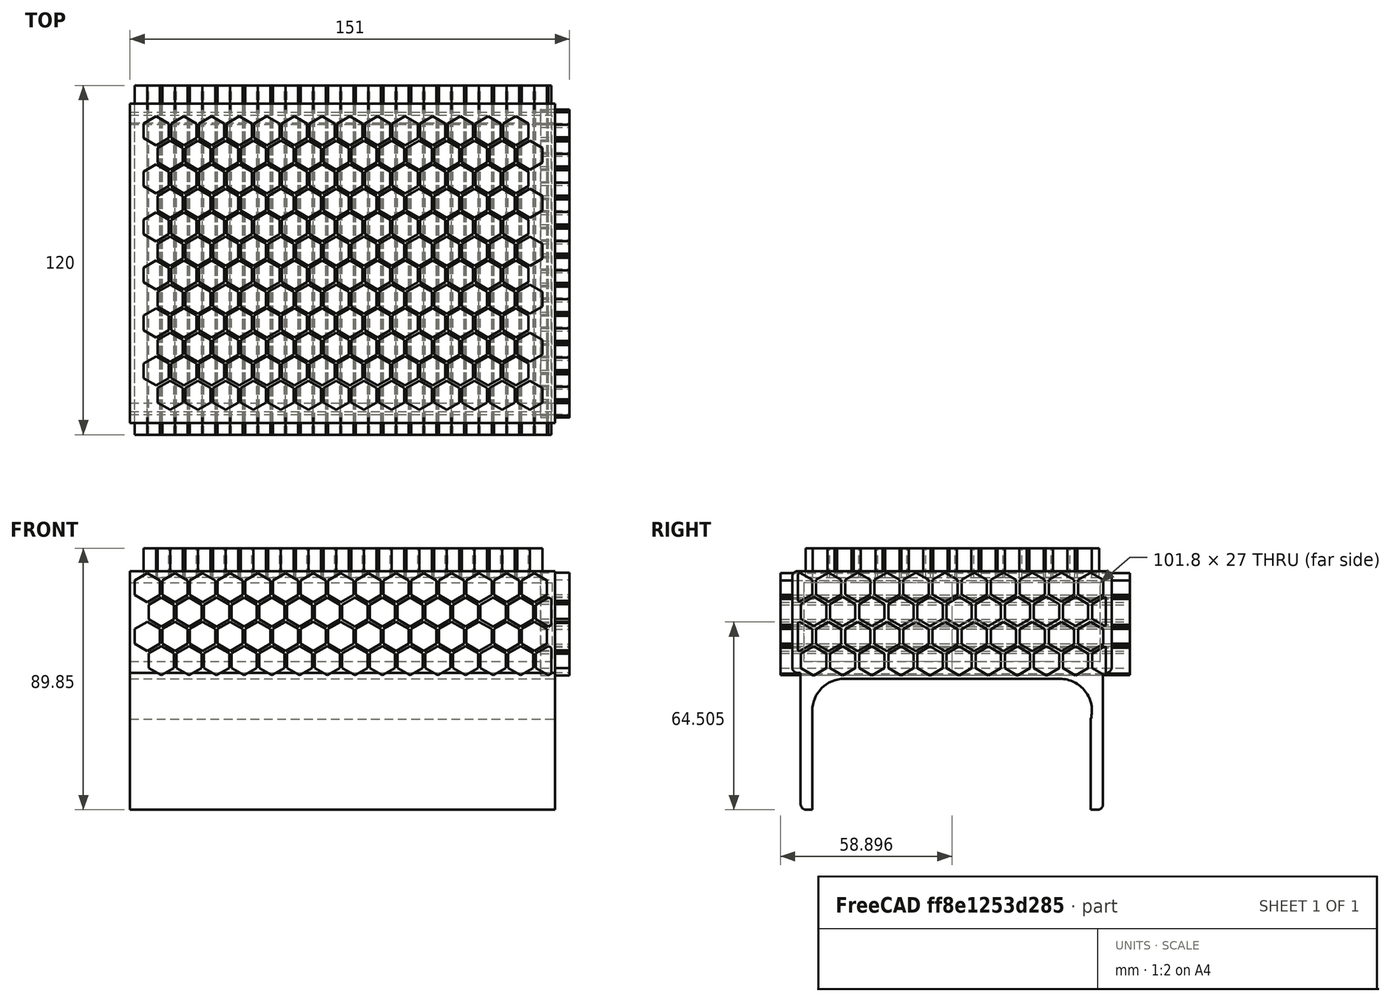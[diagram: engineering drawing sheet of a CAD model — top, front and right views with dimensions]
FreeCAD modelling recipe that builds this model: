
FCSTD DOCUMENT  (FreeCAD 1.0R39109 (Git))
Label: HDDHolder
License: All rights reserved
LicenseURL: http://en.wikipedia.org/wiki/All_rights_reserved
objects: Sketcher::SketchObject×6, Part::Extrusion×3, Spreadsheet::Sheet×2, Image::ImagePlane×2, PartDesign::Pad×2, PartDesign::Fillet×1, PartDesign::Body×1, Part::FeaturePython×1
note: 25 computed .brp shape members not serialized (recipe doc carries the construction recipe); baked Part::Feature solids carry a one-line shape summary decoded from their .brp

FEATURE [Spreadsheet::Sheet] Spreadsheet  label="Medidas"
  cells = A1='AnchoTower; B1(AnchoTower)==95.3 mm; A2='AnchoDisco; B2(AnchoDisco)==101.4 mm; A3='GrosorSoporteTower; B3(GrosorSoporteTower)==4 mm; A4='GrosorSoporteHDD; B4(GrosorSoporteHDD)==4 mm; A5='RadioAnguloTower; B5(RadioAnguloTower)==11 mm; A6='AltoSporteTower; B6(AltoSporteTower)==40 mm; A7='AltoSporteDisco; B7(AltoSporteDisco)==26 mm; A8='AltoEspacioIntermedio; B8(AltoEspacioIntermedio)==10 mm; A9='HolguraMediciones; B9(HolguraMediciones)==0.4 mm
FEATURE [Image::ImagePlane] IMG_3540
  Placement = pos=(11,-0.1,28) rot=(1,0,0;1.5708rad)
  XSize = 156.446
  YSize = 117.335
FEATURE [Sketcher::SketchObject] Sketch011
  ArcFitTolerance = 1e-06
  FullyConstrained = false
  MakeInternals = false
  Placement = pos=(147,0,0) rot=(0,1,0;1.5708rad)
  sketch-geometry (275):
    g0: LineSegment StartX=-10.1581 StartY=-48.0787 StartZ=0 EndX=-15.1581 EndY=-48.0787 EndZ=0
    g1: LineSegment StartX=-7.96737 StartY=-52.9444 StartZ=0 EndX=-7.65814 EndY=-52.4088 EndZ=0
    g2: LineSegment StartX=-7.65814 StartY=-52.4088 StartZ=0 EndX=-10.1581 EndY=-48.0787 EndZ=0
    g3: LineSegment StartX=-1.79212 StartY=-43.2485 StartZ=0 EndX=-6.79212 EndY=-43.2485 EndZ=0
    g4: LineSegment StartX=-6.79212 StartY=-43.2485 StartZ=0 EndX=-9.29212 EndY=-47.5787 EndZ=0
    g5: LineSegment StartX=-9.29212 StartY=-47.5787 StartZ=0 EndX=-6.79212 EndY=-51.9088 EndZ=0
    g6: LineSegment StartX=-6.79212 StartY=-51.9088 StartZ=0 EndX=-1.79212 EndY=-51.9088 EndZ=0
    g7: LineSegment StartX=-1.79212 StartY=-51.9088 StartZ=0 EndX=0.707884 EndY=-47.5787 EndZ=0
    g8: LineSegment StartX=0.707884 StartY=-47.5787 StartZ=0 EndX=-1.79212 EndY=-43.2485 EndZ=0
    g9: LineSegment StartX=6.84186 StartY=-48.0787 StartZ=0 EndX=1.84186 EndY=-48.0787 EndZ=0
    g10: LineSegment StartX=1.84186 StartY=-48.0787 StartZ=0 EndX=-0.658141 EndY=-52.4088 EndZ=0
    g11: LineSegment StartX=-0.658141 StartY=-52.4088 StartZ=0 EndX=-0.348916 EndY=-52.9444 EndZ=0
    g12: LineSegment StartX=9.03263 StartY=-52.9444 StartZ=0 EndX=9.34186 EndY=-52.4088 EndZ=0
    g13: LineSegment StartX=9.34186 StartY=-52.4088 StartZ=0 EndX=6.84186 EndY=-48.0787 EndZ=0
    g14: LineSegment StartX=15.2079 StartY=-43.2485 StartZ=0 EndX=10.2079 EndY=-43.2485 EndZ=0
    g15: LineSegment StartX=10.2079 StartY=-43.2485 StartZ=0 EndX=7.70788 EndY=-47.5787 EndZ=0
    g16: LineSegment StartX=7.70788 StartY=-47.5787 StartZ=0 EndX=10.2079 EndY=-51.9088 EndZ=0
    g17: LineSegment StartX=10.2079 StartY=-51.9088 StartZ=0 EndX=15.2079 EndY=-51.9088 EndZ=0
    g18: LineSegment StartX=15.2079 StartY=-51.9088 StartZ=0 EndX=17.696 EndY=-47.5993 EndZ=0
    g19: LineSegment StartX=17.696 StartY=-47.5581 StartZ=0 EndX=15.2079 EndY=-43.2485 EndZ=0
    g20: LineSegment StartX=-10.1581 StartY=-38.0787 StartZ=0 EndX=-15.1581 EndY=-38.0787 EndZ=0
    g21: LineSegment StartX=-15.1581 StartY=-38.0787 StartZ=0 EndX=-17.6581 EndY=-42.4088 EndZ=0
    g22: LineSegment StartX=-17.6581 StartY=-42.4088 StartZ=0 EndX=-15.1581 EndY=-46.7389 EndZ=0
    g23: LineSegment StartX=-15.1581 StartY=-46.7389 StartZ=0 EndX=-10.1581 EndY=-46.7389 EndZ=0
    g24: LineSegment StartX=-10.1581 StartY=-46.7389 StartZ=0 EndX=-7.65814 EndY=-42.4088 EndZ=0
    g25: LineSegment StartX=-7.65814 StartY=-42.4088 StartZ=0 EndX=-10.1581 EndY=-38.0787 EndZ=0
    g26: LineSegment StartX=-1.79212 StartY=-33.2485 StartZ=0 EndX=-6.79212 EndY=-33.2485 EndZ=0
    g27: LineSegment StartX=-6.79212 StartY=-33.2485 StartZ=0 EndX=-9.29212 EndY=-37.5787 EndZ=0
    g28: LineSegment StartX=-9.29212 StartY=-37.5787 StartZ=0 EndX=-6.79212 EndY=-41.9088 EndZ=0
    g29: LineSegment StartX=-6.79212 StartY=-41.9088 StartZ=0 EndX=-1.79212 EndY=-41.9088 EndZ=0
    g30: LineSegment StartX=-1.79212 StartY=-41.9088 StartZ=0 EndX=0.707884 EndY=-37.5787 EndZ=0
    g31: LineSegment StartX=0.707884 StartY=-37.5787 StartZ=0 EndX=-1.79212 EndY=-33.2485 EndZ=0
    g32: LineSegment StartX=6.84186 StartY=-38.0787 StartZ=0 EndX=1.84186 EndY=-38.0787 EndZ=0
    g33: LineSegment StartX=1.84186 StartY=-38.0787 StartZ=0 EndX=-0.658141 EndY=-42.4088 EndZ=0
    g34: LineSegment StartX=-0.658141 StartY=-42.4088 StartZ=0 EndX=1.84186 EndY=-46.7389 EndZ=0
    g35: LineSegment StartX=1.84186 StartY=-46.7389 StartZ=0 EndX=6.84186 EndY=-46.7389 EndZ=0
    g36: LineSegment StartX=6.84186 StartY=-46.7389 StartZ=0 EndX=9.34186 EndY=-42.4088 EndZ=0
    g37: LineSegment StartX=9.34186 StartY=-42.4088 StartZ=0 EndX=6.84186 EndY=-38.0787 EndZ=0
    g38: LineSegment StartX=15.2079 StartY=-33.2485 StartZ=0 EndX=10.2079 EndY=-33.2485 EndZ=0
    g39: LineSegment StartX=10.2079 StartY=-33.2485 StartZ=0 EndX=7.70788 EndY=-37.5787 EndZ=0
    g40: LineSegment StartX=7.70788 StartY=-37.5787 StartZ=0 EndX=10.2079 EndY=-41.9088 EndZ=0
    g41: LineSegment StartX=10.2079 StartY=-41.9088 StartZ=0 EndX=15.2079 EndY=-41.9088 EndZ=0
    g42: LineSegment StartX=15.2079 StartY=-41.9088 StartZ=0 EndX=17.696 EndY=-37.5993 EndZ=0
    g43: LineSegment StartX=17.696 StartY=-37.5581 StartZ=0 EndX=15.2079 EndY=-33.2485 EndZ=0
    g44: LineSegment StartX=-10.1581 StartY=-28.0787 StartZ=0 EndX=-15.1581 EndY=-28.0787 EndZ=0
    g45: LineSegment StartX=-15.1581 StartY=-28.0787 StartZ=0 EndX=-17.6581 EndY=-32.4088 EndZ=0
    g46: LineSegment StartX=-17.6581 StartY=-32.4088 StartZ=0 EndX=-15.1581 EndY=-36.7389 EndZ=0
    g47: LineSegment StartX=-15.1581 StartY=-36.7389 StartZ=0 EndX=-10.1581 EndY=-36.7389 EndZ=0
    g48: LineSegment StartX=-10.1581 StartY=-36.7389 StartZ=0 EndX=-7.65814 EndY=-32.4088 EndZ=0
    g49: LineSegment StartX=-7.65814 StartY=-32.4088 StartZ=0 EndX=-10.1581 EndY=-28.0787 EndZ=0
    g50: LineSegment StartX=-1.79212 StartY=-23.2485 StartZ=0 EndX=-6.79212 EndY=-23.2485 EndZ=0
    g51: LineSegment StartX=-6.79212 StartY=-23.2485 StartZ=0 EndX=-9.29212 EndY=-27.5787 EndZ=0
    g52: LineSegment StartX=-9.29212 StartY=-27.5787 StartZ=0 EndX=-6.79212 EndY=-31.9088 EndZ=0
    g53: LineSegment StartX=-6.79212 StartY=-31.9088 StartZ=0 EndX=-1.79212 EndY=-31.9088 EndZ=0
    g54: LineSegment StartX=-1.79212 StartY=-31.9088 StartZ=0 EndX=0.707884 EndY=-27.5787 EndZ=0
    g55: LineSegment StartX=0.707884 StartY=-27.5787 StartZ=0 EndX=-1.79212 EndY=-23.2485 EndZ=0
    g56: LineSegment StartX=6.84186 StartY=-28.0787 StartZ=0 EndX=1.84186 EndY=-28.0787 EndZ=0
    g57: LineSegment StartX=1.84186 StartY=-28.0787 StartZ=0 EndX=-0.658141 EndY=-32.4088 EndZ=0
    g58: LineSegment StartX=-0.658141 StartY=-32.4088 StartZ=0 EndX=1.84186 EndY=-36.7389 EndZ=0
    g59: LineSegment StartX=1.84186 StartY=-36.7389 StartZ=0 EndX=6.84186 EndY=-36.7389 EndZ=0
    g60: LineSegment StartX=6.84186 StartY=-36.7389 StartZ=0 EndX=9.34186 EndY=-32.4088 EndZ=0
    g61: LineSegment StartX=9.34186 StartY=-32.4088 StartZ=0 EndX=6.84186 EndY=-28.0787 EndZ=0
    g62: LineSegment StartX=15.2079 StartY=-23.2485 StartZ=0 EndX=10.2079 EndY=-23.2485 EndZ=0
    g63: LineSegment StartX=10.2079 StartY=-23.2485 StartZ=0 EndX=7.70788 EndY=-27.5787 EndZ=0
    g64: LineSegment StartX=7.70788 StartY=-27.5787 StartZ=0 EndX=10.2079 EndY=-31.9088 EndZ=0
    g65: LineSegment StartX=10.2079 StartY=-31.9088 StartZ=0 EndX=15.2079 EndY=-31.9088 EndZ=0
    g66: LineSegment StartX=15.2079 StartY=-31.9088 StartZ=0 EndX=17.696 EndY=-27.5993 EndZ=0
    g67: LineSegment StartX=17.696 StartY=-27.5581 StartZ=0 EndX=15.2079 EndY=-23.2485 EndZ=0
    g68: LineSegment StartX=-10.1581 StartY=-18.0787 StartZ=0 EndX=-15.1581 EndY=-18.0787 EndZ=0
    g69: LineSegment StartX=-15.1581 StartY=-18.0787 StartZ=0 EndX=-17.6581 EndY=-22.4088 EndZ=0
    g70: LineSegment StartX=-17.6581 StartY=-22.4088 StartZ=0 EndX=-15.1581 EndY=-26.7389 EndZ=0
    g71: LineSegment StartX=-15.1581 StartY=-26.7389 StartZ=0 EndX=-10.1581 EndY=-26.7389 EndZ=0
    g72: LineSegment StartX=-10.1581 StartY=-26.7389 StartZ=0 EndX=-7.65814 EndY=-22.4088 EndZ=0
    g73: LineSegment StartX=-7.65814 StartY=-22.4088 StartZ=0 EndX=-10.1581 EndY=-18.0787 EndZ=0
    g74: LineSegment StartX=-1.79212 StartY=-13.2485 StartZ=0 EndX=-6.79212 EndY=-13.2485 EndZ=0
    g75: LineSegment StartX=-6.79212 StartY=-13.2485 StartZ=0 EndX=-9.29212 EndY=-17.5787 EndZ=0
    g76: LineSegment StartX=-9.29212 StartY=-17.5787 StartZ=0 EndX=-6.79212 EndY=-21.9088 EndZ=0
    g77: LineSegment StartX=-6.79212 StartY=-21.9088 StartZ=0 EndX=-1.79212 EndY=-21.9088 EndZ=0
    g78: LineSegment StartX=-1.79212 StartY=-21.9088 StartZ=0 EndX=0.707884 EndY=-17.5787 EndZ=0
    g79: LineSegment StartX=0.707884 StartY=-17.5787 StartZ=0 EndX=-1.79212 EndY=-13.2485 EndZ=0
    g80: LineSegment StartX=6.84186 StartY=-18.0787 StartZ=0 EndX=1.84186 EndY=-18.0787 EndZ=0
    g81: LineSegment StartX=1.84186 StartY=-18.0787 StartZ=0 EndX=-0.658141 EndY=-22.4088 EndZ=0
    g82: LineSegment StartX=-0.658141 StartY=-22.4088 StartZ=0 EndX=1.84186 EndY=-26.7389 EndZ=0
    g83: LineSegment StartX=1.84186 StartY=-26.7389 StartZ=0 EndX=6.84186 EndY=-26.7389 EndZ=0
    g84: LineSegment StartX=6.84186 StartY=-26.7389 StartZ=0 EndX=9.34186 EndY=-22.4088 EndZ=0
    g85: LineSegment StartX=9.34186 StartY=-22.4088 StartZ=0 EndX=6.84186 EndY=-18.0787 EndZ=0
    g86: LineSegment StartX=15.2079 StartY=-13.2485 StartZ=0 EndX=10.2079 EndY=-13.2485 EndZ=0
    g87: LineSegment StartX=10.2079 StartY=-13.2485 StartZ=0 EndX=7.70788 EndY=-17.5787 EndZ=0
    g88: LineSegment StartX=7.70788 StartY=-17.5787 StartZ=0 EndX=10.2079 EndY=-21.9088 EndZ=0
    g89: LineSegment StartX=10.2079 StartY=-21.9088 StartZ=0 EndX=15.2079 EndY=-21.9088 EndZ=0
    g90: LineSegment StartX=15.2079 StartY=-21.9088 StartZ=0 EndX=17.696 EndY=-17.5993 EndZ=0
    g91: LineSegment StartX=17.696 StartY=-17.5581 StartZ=0 EndX=15.2079 EndY=-13.2485 EndZ=0
    g92: LineSegment StartX=-10.1581 StartY=-8.07867 StartZ=0 EndX=-15.1581 EndY=-8.07867 EndZ=0
    g93: LineSegment StartX=-15.1581 StartY=-8.07867 StartZ=0 EndX=-17.6581 EndY=-12.4088 EndZ=0
    g94: LineSegment StartX=-17.6581 StartY=-12.4088 StartZ=0 EndX=-15.1581 EndY=-16.7389 EndZ=0
    g95: LineSegment StartX=-15.1581 StartY=-16.7389 StartZ=0 EndX=-10.1581 EndY=-16.7389 EndZ=0
    g96: LineSegment StartX=-10.1581 StartY=-16.7389 StartZ=0 EndX=-7.65814 EndY=-12.4088 EndZ=0
    g97: LineSegment StartX=-7.65814 StartY=-12.4088 StartZ=0 EndX=-10.1581 EndY=-8.07867 EndZ=0
    g98: LineSegment StartX=-1.79212 StartY=-3.24855 StartZ=0 EndX=-6.79212 EndY=-3.24855 EndZ=0
    g99: LineSegment StartX=-6.79212 StartY=-3.24855 StartZ=0 EndX=-9.29212 EndY=-7.57867 EndZ=0
    g100: LineSegment StartX=-9.29212 StartY=-7.57867 StartZ=0 EndX=-6.79212 EndY=-11.9088 EndZ=0
    g101: LineSegment StartX=-6.79212 StartY=-11.9088 StartZ=0 EndX=-1.79212 EndY=-11.9088 EndZ=0
    g102: LineSegment StartX=-1.79212 StartY=-11.9088 StartZ=0 EndX=0.707884 EndY=-7.57867 EndZ=0
    g103: LineSegment StartX=0.707884 StartY=-7.57867 StartZ=0 EndX=-1.79212 EndY=-3.24855 EndZ=0
    g104: LineSegment StartX=6.84186 StartY=-8.07867 StartZ=0 EndX=1.84186 EndY=-8.07867 EndZ=0
    g105: LineSegment StartX=1.84186 StartY=-8.07867 StartZ=0 EndX=-0.658141 EndY=-12.4088 EndZ=0
    g106: LineSegment StartX=-0.658141 StartY=-12.4088 StartZ=0 EndX=1.84186 EndY=-16.7389 EndZ=0
    g107: LineSegment StartX=1.84186 StartY=-16.7389 StartZ=0 EndX=6.84186 EndY=-16.7389 EndZ=0
    g108: LineSegment StartX=6.84186 StartY=-16.7389 StartZ=0 EndX=9.34186 EndY=-12.4088 EndZ=0
    g109: LineSegment StartX=9.34186 StartY=-12.4088 StartZ=0 EndX=6.84186 EndY=-8.07867 EndZ=0
    g110: LineSegment StartX=15.2079 StartY=-3.24855 StartZ=0 EndX=10.2079 EndY=-3.24855 EndZ=0
    g111: LineSegment StartX=10.2079 StartY=-3.24855 StartZ=0 EndX=7.70788 EndY=-7.57867 EndZ=0
    g112: LineSegment StartX=7.70788 StartY=-7.57867 StartZ=0 EndX=10.2079 EndY=-11.9088 EndZ=0
    g113: LineSegment StartX=10.2079 StartY=-11.9088 StartZ=0 EndX=15.2079 EndY=-11.9088 EndZ=0
    g114: LineSegment StartX=15.2079 StartY=-11.9088 StartZ=0 EndX=17.696 EndY=-7.59926 EndZ=0
    g115: LineSegment StartX=17.696 StartY=-7.55809 StartZ=0 EndX=15.2079 EndY=-3.24855 EndZ=0
    g116: LineSegment StartX=-10.1581 StartY=1.92133 StartZ=0 EndX=-15.1581 EndY=1.92133 EndZ=0
    g117: LineSegment StartX=-15.1581 StartY=1.92133 StartZ=0 EndX=-17.6581 EndY=-2.4088 EndZ=0
    g118: LineSegment StartX=-17.6581 StartY=-2.4088 StartZ=0 EndX=-15.1581 EndY=-6.73893 EndZ=0
    g119: LineSegment StartX=-15.1581 StartY=-6.73893 StartZ=0 EndX=-10.1581 EndY=-6.73893 EndZ=0
    g120: LineSegment StartX=-10.1581 StartY=-6.73893 StartZ=0 EndX=-7.65814 EndY=-2.4088 EndZ=0
    g121: LineSegment StartX=-7.65814 StartY=-2.4088 StartZ=0 EndX=-10.1581 EndY=1.92133 EndZ=0
    g122: LineSegment StartX=-1.79212 StartY=6.75145 StartZ=0 EndX=-6.79212 EndY=6.75145 EndZ=0
    g123: LineSegment StartX=-6.79212 StartY=6.75145 StartZ=0 EndX=-9.29212 EndY=2.42133 EndZ=0
    g124: LineSegment StartX=-9.29212 StartY=2.42133 StartZ=0 EndX=-6.79212 EndY=-1.9088 EndZ=0
    g125: LineSegment StartX=-6.79212 StartY=-1.9088 StartZ=0 EndX=-1.79212 EndY=-1.9088 EndZ=0
    g126: LineSegment StartX=-1.79212 StartY=-1.9088 StartZ=0 EndX=0.707884 EndY=2.42133 EndZ=0
    g127: LineSegment StartX=0.707884 StartY=2.42133 StartZ=0 EndX=-1.79212 EndY=6.75145 EndZ=0
    g128: LineSegment StartX=6.84186 StartY=1.92133 StartZ=0 EndX=1.84186 EndY=1.92133 EndZ=0
    g129: LineSegment StartX=1.84186 StartY=1.92133 StartZ=0 EndX=-0.658141 EndY=-2.4088 EndZ=0
    g130: LineSegment StartX=-0.658141 StartY=-2.4088 StartZ=0 EndX=1.84186 EndY=-6.73893 EndZ=0
    g131: LineSegment StartX=1.84186 StartY=-6.73893 StartZ=0 EndX=6.84186 EndY=-6.73893 EndZ=0
    g132: LineSegment StartX=6.84186 StartY=-6.73893 StartZ=0 EndX=9.34186 EndY=-2.4088 EndZ=0
    g133: LineSegment StartX=9.34186 StartY=-2.4088 StartZ=0 EndX=6.84186 EndY=1.92133 EndZ=0
    g134: LineSegment StartX=15.2079 StartY=6.75145 StartZ=0 EndX=10.2079 EndY=6.75145 EndZ=0
    g135: LineSegment StartX=10.2079 StartY=6.75145 StartZ=0 EndX=7.70788 EndY=2.42133 EndZ=0
    g136: LineSegment StartX=7.70788 StartY=2.42133 StartZ=0 EndX=10.2079 EndY=-1.9088 EndZ=0
    g137: LineSegment StartX=10.2079 StartY=-1.9088 StartZ=0 EndX=15.2079 EndY=-1.9088 EndZ=0
    g138: LineSegment StartX=15.2079 StartY=-1.9088 StartZ=0 EndX=17.696 EndY=2.40074 EndZ=0
    g139: LineSegment StartX=17.696 StartY=2.44191 StartZ=0 EndX=15.2079 EndY=6.75145 EndZ=0
    g140: LineSegment StartX=-10.1581 StartY=11.9213 StartZ=0 EndX=-15.1581 EndY=11.9213 EndZ=0
    g141: LineSegment StartX=-15.1581 StartY=11.9213 StartZ=0 EndX=-17.6581 EndY=7.5912 EndZ=0
    g142: LineSegment StartX=-17.6581 StartY=7.5912 StartZ=0 EndX=-15.1581 EndY=3.26107 EndZ=0
    g143: LineSegment StartX=-15.1581 StartY=3.26107 StartZ=0 EndX=-10.1581 EndY=3.26107 EndZ=0
    g144: LineSegment StartX=-10.1581 StartY=3.26107 StartZ=0 EndX=-7.65814 EndY=7.5912 EndZ=0
    g145: LineSegment StartX=-7.65814 StartY=7.5912 StartZ=0 EndX=-10.1581 EndY=11.9213 EndZ=0
    g146: LineSegment StartX=-1.79212 StartY=16.7515 StartZ=0 EndX=-6.79212 EndY=16.7515 EndZ=0
    g147: LineSegment StartX=-6.79212 StartY=16.7515 StartZ=0 EndX=-9.29212 EndY=12.4213 EndZ=0
    g148: LineSegment StartX=-9.29212 StartY=12.4213 StartZ=0 EndX=-6.79212 EndY=8.0912 EndZ=0
    g149: LineSegment StartX=-6.79212 StartY=8.0912 StartZ=0 EndX=-1.79212 EndY=8.0912 EndZ=0
    g150: LineSegment StartX=-1.79212 StartY=8.0912 StartZ=0 EndX=0.707884 EndY=12.4213 EndZ=0
    g151: LineSegment StartX=0.707884 StartY=12.4213 StartZ=0 EndX=-1.79212 EndY=16.7515 EndZ=0
    g152: LineSegment StartX=6.84186 StartY=11.9213 StartZ=0 EndX=1.84186 EndY=11.9213 EndZ=0
    g153: LineSegment StartX=1.84186 StartY=11.9213 StartZ=0 EndX=-0.658141 EndY=7.5912 EndZ=0
    g154: LineSegment StartX=-0.658141 StartY=7.5912 StartZ=0 EndX=1.84186 EndY=3.26107 EndZ=0
    g155: LineSegment StartX=1.84186 StartY=3.26107 StartZ=0 EndX=6.84186 EndY=3.26107 EndZ=0
    g156: LineSegment StartX=6.84186 StartY=3.26107 StartZ=0 EndX=9.34186 EndY=7.5912 EndZ=0
    g157: LineSegment StartX=9.34186 StartY=7.5912 StartZ=0 EndX=6.84186 EndY=11.9213 EndZ=0
    g158: LineSegment StartX=15.2079 StartY=16.7515 StartZ=0 EndX=10.2079 EndY=16.7515 EndZ=0
    g159: LineSegment StartX=10.2079 StartY=16.7515 StartZ=0 EndX=7.70788 EndY=12.4213 EndZ=0
    g160: LineSegment StartX=7.70788 StartY=12.4213 StartZ=0 EndX=10.2079 EndY=8.0912 EndZ=0
    g161: LineSegment StartX=10.2079 StartY=8.0912 StartZ=0 EndX=15.2079 EndY=8.0912 EndZ=0
    g162: LineSegment StartX=15.2079 StartY=8.0912 StartZ=0 EndX=17.696 EndY=12.4007 EndZ=0
    g163: LineSegment StartX=17.696 StartY=12.4419 StartZ=0 EndX=15.2079 EndY=16.7515 EndZ=0
    g164: LineSegment StartX=-10.1581 StartY=21.9213 StartZ=0 EndX=-15.1581 EndY=21.9213 EndZ=0
    g165: LineSegment StartX=-15.1581 StartY=21.9213 StartZ=0 EndX=-17.6581 EndY=17.5912 EndZ=0
    g166: LineSegment StartX=-17.6581 StartY=17.5912 StartZ=0 EndX=-15.1581 EndY=13.2611 EndZ=0
    g167: LineSegment StartX=-15.1581 StartY=13.2611 StartZ=0 EndX=-10.1581 EndY=13.2611 EndZ=0
    g168: LineSegment StartX=-10.1581 StartY=13.2611 StartZ=0 EndX=-7.65814 EndY=17.5912 EndZ=0
    g169: LineSegment StartX=-7.65814 StartY=17.5912 StartZ=0 EndX=-10.1581 EndY=21.9213 EndZ=0
    g170: LineSegment StartX=-1.79212 StartY=26.7515 StartZ=0 EndX=-6.79212 EndY=26.7515 EndZ=0
    g171: LineSegment StartX=-6.79212 StartY=26.7515 StartZ=0 EndX=-9.29212 EndY=22.4213 EndZ=0
    g172: LineSegment StartX=-9.29212 StartY=22.4213 StartZ=0 EndX=-6.79212 EndY=18.0912 EndZ=0
    g173: LineSegment StartX=-6.79212 StartY=18.0912 StartZ=0 EndX=-1.79212 EndY=18.0912 EndZ=0
    g174: LineSegment StartX=-1.79212 StartY=18.0912 StartZ=0 EndX=0.707884 EndY=22.4213 EndZ=0
    g175: LineSegment StartX=0.707884 StartY=22.4213 StartZ=0 EndX=-1.79212 EndY=26.7515 EndZ=0
    g176: LineSegment StartX=6.84186 StartY=21.9213 StartZ=0 EndX=1.84186 EndY=21.9213 EndZ=0
    g177: LineSegment StartX=1.84186 StartY=21.9213 StartZ=0 EndX=-0.658141 EndY=17.5912 EndZ=0
    g178: LineSegment StartX=-0.658141 StartY=17.5912 StartZ=0 EndX=1.84186 EndY=13.2611 EndZ=0
    g179: LineSegment StartX=1.84186 StartY=13.2611 StartZ=0 EndX=6.84186 EndY=13.2611 EndZ=0
    g180: LineSegment StartX=6.84186 StartY=13.2611 StartZ=0 EndX=9.34186 EndY=17.5912 EndZ=0
    g181: LineSegment StartX=9.34186 StartY=17.5912 StartZ=0 EndX=6.84186 EndY=21.9213 EndZ=0
    g182: LineSegment StartX=15.2079 StartY=26.7515 StartZ=0 EndX=10.2079 EndY=26.7515 EndZ=0
    g183: LineSegment StartX=10.2079 StartY=26.7515 StartZ=0 EndX=7.70788 EndY=22.4213 EndZ=0
    g184: LineSegment StartX=7.70788 StartY=22.4213 StartZ=0 EndX=10.2079 EndY=18.0912 EndZ=0
    g185: LineSegment StartX=10.2079 StartY=18.0912 StartZ=0 EndX=15.2079 EndY=18.0912 EndZ=0
    g186: LineSegment StartX=15.2079 StartY=18.0912 StartZ=0 EndX=17.696 EndY=22.4007 EndZ=0
    g187: LineSegment StartX=17.696 StartY=22.4419 StartZ=0 EndX=15.2079 EndY=26.7515 EndZ=0
    g188: LineSegment StartX=-10.1581 StartY=31.9213 StartZ=0 EndX=-15.1581 EndY=31.9213 EndZ=0
    g189: LineSegment StartX=-15.1581 StartY=31.9213 StartZ=0 EndX=-17.6581 EndY=27.5912 EndZ=0
    g190: LineSegment StartX=-17.6581 StartY=27.5912 StartZ=0 EndX=-15.1581 EndY=23.2611 EndZ=0
    g191: LineSegment StartX=-15.1581 StartY=23.2611 StartZ=0 EndX=-10.1581 EndY=23.2611 EndZ=0
    g192: LineSegment StartX=-10.1581 StartY=23.2611 StartZ=0 EndX=-7.65814 EndY=27.5912 EndZ=0
    g193: LineSegment StartX=-7.65814 StartY=27.5912 StartZ=0 EndX=-10.1581 EndY=31.9213 EndZ=0
    g194: LineSegment StartX=-1.79212 StartY=36.7515 StartZ=0 EndX=-6.79212 EndY=36.7515 EndZ=0
    g195: LineSegment StartX=-6.79212 StartY=36.7515 StartZ=0 EndX=-9.29212 EndY=32.4213 EndZ=0
    g196: LineSegment StartX=-9.29212 StartY=32.4213 StartZ=0 EndX=-6.79212 EndY=28.0912 EndZ=0
    g197: LineSegment StartX=-6.79212 StartY=28.0912 StartZ=0 EndX=-1.79212 EndY=28.0912 EndZ=0
    g198: LineSegment StartX=-1.79212 StartY=28.0912 StartZ=0 EndX=0.707884 EndY=32.4213 EndZ=0
    g199: LineSegment StartX=0.707884 StartY=32.4213 StartZ=0 EndX=-1.79212 EndY=36.7515 EndZ=0
    g200: LineSegment StartX=6.84186 StartY=31.9213 StartZ=0 EndX=1.84186 EndY=31.9213 EndZ=0
    g201: LineSegment StartX=1.84186 StartY=31.9213 StartZ=0 EndX=-0.658141 EndY=27.5912 EndZ=0
    g202: LineSegment StartX=-0.658141 StartY=27.5912 StartZ=0 EndX=1.84186 EndY=23.2611 EndZ=0
    g203: LineSegment StartX=1.84186 StartY=23.2611 StartZ=0 EndX=6.84186 EndY=23.2611 EndZ=0
    g204: LineSegment StartX=6.84186 StartY=23.2611 StartZ=0 EndX=9.34186 EndY=27.5912 EndZ=0
    g205: LineSegment StartX=9.34186 StartY=27.5912 StartZ=0 EndX=6.84186 EndY=31.9213 EndZ=0
    g206: LineSegment StartX=15.2079 StartY=36.7515 StartZ=0 EndX=10.2079 EndY=36.7515 EndZ=0
    g207: LineSegment StartX=10.2079 StartY=36.7515 StartZ=0 EndX=7.70788 EndY=32.4213 EndZ=0
    g208: LineSegment StartX=7.70788 StartY=32.4213 StartZ=0 EndX=10.2079 EndY=28.0912 EndZ=0
    g209: LineSegment StartX=10.2079 StartY=28.0912 StartZ=0 EndX=15.2079 EndY=28.0912 EndZ=0
    g210: LineSegment StartX=15.2079 StartY=28.0912 StartZ=0 EndX=17.696 EndY=32.4007 EndZ=0
    g211: LineSegment StartX=17.696 StartY=32.4419 StartZ=0 EndX=15.2079 EndY=36.7515 EndZ=0
    g212: LineSegment StartX=-10.1581 StartY=41.9213 StartZ=0 EndX=-15.1581 EndY=41.9213 EndZ=0
    g213: LineSegment StartX=-15.1581 StartY=41.9213 StartZ=0 EndX=-17.6581 EndY=37.5912 EndZ=0
    g214: LineSegment StartX=-17.6581 StartY=37.5912 StartZ=0 EndX=-15.1581 EndY=33.2611 EndZ=0
    g215: LineSegment StartX=-15.1581 StartY=33.2611 StartZ=0 EndX=-10.1581 EndY=33.2611 EndZ=0
    g216: LineSegment StartX=-10.1581 StartY=33.2611 StartZ=0 EndX=-7.65814 EndY=37.5912 EndZ=0
    g217: LineSegment StartX=-7.65814 StartY=37.5912 StartZ=0 EndX=-10.1581 EndY=41.9213 EndZ=0
    g218: LineSegment StartX=-1.79212 StartY=46.7515 StartZ=0 EndX=-6.79212 EndY=46.7515 EndZ=0
    g219: LineSegment StartX=-6.79212 StartY=46.7515 StartZ=0 EndX=-9.29212 EndY=42.4213 EndZ=0
    g220: LineSegment StartX=-9.29212 StartY=42.4213 StartZ=0 EndX=-6.79212 EndY=38.0912 EndZ=0
    g221: LineSegment StartX=-6.79212 StartY=38.0912 StartZ=0 EndX=-1.79212 EndY=38.0912 EndZ=0
    g222: LineSegment StartX=-1.79212 StartY=38.0912 StartZ=0 EndX=0.707884 EndY=42.4213 EndZ=0
    g223: LineSegment StartX=0.707884 StartY=42.4213 StartZ=0 EndX=-1.79212 EndY=46.7515 EndZ=0
    g224: LineSegment StartX=6.84186 StartY=41.9213 StartZ=0 EndX=1.84186 EndY=41.9213 EndZ=0
    g225: LineSegment StartX=1.84186 StartY=41.9213 StartZ=0 EndX=-0.658141 EndY=37.5912 EndZ=0
    g226: LineSegment StartX=-0.658141 StartY=37.5912 StartZ=0 EndX=1.84186 EndY=33.2611 EndZ=0
    g227: LineSegment StartX=1.84186 StartY=33.2611 StartZ=0 EndX=6.84186 EndY=33.2611 EndZ=0
    g228: LineSegment StartX=6.84186 StartY=33.2611 StartZ=0 EndX=9.34186 EndY=37.5912 EndZ=0
    g229: LineSegment StartX=9.34186 StartY=37.5912 StartZ=0 EndX=6.84186 EndY=41.9213 EndZ=0
    g230: LineSegment StartX=15.2079 StartY=46.7515 StartZ=0 EndX=10.2079 EndY=46.7515 EndZ=0
    g231: LineSegment StartX=10.2079 StartY=46.7515 StartZ=0 EndX=7.70788 EndY=42.4213 EndZ=0
    g232: LineSegment StartX=7.70788 StartY=42.4213 StartZ=0 EndX=10.2079 EndY=38.0912 EndZ=0
    g233: LineSegment StartX=10.2079 StartY=38.0912 StartZ=0 EndX=15.2079 EndY=38.0912 EndZ=0
    g234: LineSegment StartX=15.2079 StartY=38.0912 StartZ=0 EndX=17.696 EndY=42.4007 EndZ=0
    g235: LineSegment StartX=-10.1581 StartY=51.9213 StartZ=0 EndX=-15.1581 EndY=51.9213 EndZ=0
    g236: LineSegment StartX=-15.1581 StartY=51.9213 StartZ=0 EndX=-17.6581 EndY=47.5912 EndZ=0
    g237: LineSegment StartX=-17.6581 StartY=47.5912 StartZ=0 EndX=-15.1581 EndY=43.2611 EndZ=0
    g238: LineSegment StartX=-15.1581 StartY=43.2611 StartZ=0 EndX=-10.1581 EndY=43.2611 EndZ=0
    g239: LineSegment StartX=-10.1581 StartY=43.2611 StartZ=0 EndX=-7.65814 EndY=47.5912 EndZ=0
    g240: LineSegment StartX=-7.65814 StartY=47.5912 StartZ=0 EndX=-10.1581 EndY=51.9213 EndZ=0
    g241: LineSegment StartX=-9.29212 StartY=52.4213 StartZ=0 EndX=-6.79212 EndY=48.0912 EndZ=0
    g242: LineSegment StartX=-6.79212 StartY=48.0912 StartZ=0 EndX=-1.79212 EndY=48.0912 EndZ=0
    g243: LineSegment StartX=-1.79212 StartY=48.0912 StartZ=0 EndX=0.707884 EndY=52.4213 EndZ=0
    g244: LineSegment StartX=0.707884 StartY=52.4213 StartZ=0 EndX=0.457153 EndY=52.8556 EndZ=0
    g245: LineSegment StartX=6.84186 StartY=51.9213 StartZ=0 EndX=1.84186 EndY=51.9213 EndZ=0
    g246: LineSegment StartX=1.84186 StartY=51.9213 StartZ=0 EndX=-0.658141 EndY=47.5912 EndZ=0
    g247: LineSegment StartX=-0.658141 StartY=47.5912 StartZ=0 EndX=1.84186 EndY=43.2611 EndZ=0
    g248: LineSegment StartX=1.84186 StartY=43.2611 StartZ=0 EndX=6.84186 EndY=43.2611 EndZ=0
    g249: LineSegment StartX=6.84186 StartY=43.2611 StartZ=0 EndX=9.34186 EndY=47.5912 EndZ=0
    g250: LineSegment StartX=9.34186 StartY=47.5912 StartZ=0 EndX=6.84186 EndY=51.9213 EndZ=0
    g251: LineSegment StartX=7.70788 StartY=52.4213 StartZ=0 EndX=10.2079 EndY=48.0912 EndZ=0
    g252: LineSegment StartX=10.2079 StartY=48.0912 StartZ=0 EndX=15.2079 EndY=48.0912 EndZ=0
    g253: LineSegment StartX=15.2079 StartY=48.0912 StartZ=0 EndX=17.6124 EndY=52.2559 EndZ=0
    g254: LineSegment [constr] StartX=-9.04139 StartY=52.8556 StartZ=0 EndX=0.457153 EndY=52.8556 EndZ=0
    g255: LineSegment StartX=17.696 StartY=42.4419 StartZ=0 EndX=17.696 EndY=42.4007 EndZ=0
    g256: LineSegment StartX=-9.04139 StartY=52.8556 StartZ=0 EndX=0.457153 EndY=52.8556 EndZ=0
    g257: LineSegment StartX=7.95861 StartY=52.8556 StartZ=0 EndX=16.696 EndY=52.8556 EndZ=0
    g258: LineSegment StartX=17.696 StartY=32.4419 StartZ=0 EndX=17.696 EndY=32.4007 EndZ=0
    g259: LineSegment StartX=17.696 StartY=22.4419 StartZ=0 EndX=17.696 EndY=22.4007 EndZ=0
    g260: LineSegment StartX=17.696 StartY=12.4419 StartZ=0 EndX=17.696 EndY=12.4007 EndZ=0
    g261: LineSegment StartX=17.696 StartY=2.44191 StartZ=0 EndX=17.696 EndY=2.40074 EndZ=0
    g262: LineSegment StartX=17.696 StartY=-7.55809 StartZ=0 EndX=17.696 EndY=-7.59926 EndZ=0
    g263: LineSegment StartX=17.696 StartY=-17.5581 StartZ=0 EndX=17.696 EndY=-17.5993 EndZ=0
    g264: LineSegment StartX=17.696 StartY=-27.5581 StartZ=0 EndX=17.696 EndY=-27.5993 EndZ=0
    g265: LineSegment StartX=17.696 StartY=-37.5581 StartZ=0 EndX=17.696 EndY=-37.5993 EndZ=0
    g266: LineSegment StartX=17.696 StartY=-47.5581 StartZ=0 EndX=17.696 EndY=-47.5993 EndZ=0
    g267: LineSegment StartX=-9.29212 StartY=52.4213 StartZ=0 EndX=-9.04139 EndY=52.8556 EndZ=0
    g268: LineSegment StartX=15.2079 StartY=46.7515 StartZ=0 EndX=17.696 EndY=42.4419 EndZ=0
    g269: LineSegment StartX=-0.348916 StartY=-52.9444 StartZ=0 EndX=9.03263 EndY=-52.9444 EndZ=0
    g270: ArcOfCircle CenterX=-16.6843 CenterY=-51.9297 CenterZ=0 NormalX=0 NormalY=0 NormalZ=1 AngleXU=0 Radius=1.01473 StartAngle=3.55141 EndAngle=4.7028
    g271: LineSegment StartX=-16.694 StartY=-52.9444 StartZ=0 EndX=-7.96737 EndY=-52.9444 EndZ=0
    g272: LineSegment StartX=-17.615 StartY=-52.334 StartZ=0 EndX=-15.1581 EndY=-48.0787 EndZ=0
    g273: LineSegment StartX=7.70788 StartY=52.4213 StartZ=0 EndX=7.95861 EndY=52.8556 EndZ=0
    g274: ArcOfCircle CenterX=16.7088 CenterY=51.8751 CenterZ=0 NormalX=0 NormalY=0 NormalZ=1 AngleXU=0 Radius=0.98054 StartAngle=0.398803 EndAngle=1.58384
  constraints (362):
    c: Horizontal(g0)
    c: Coincident(g1,g2)
    c: Coincident(g2,g0)
    c: Horizontal(g3)
    c: Coincident(g3,g4)
    c: Coincident(g4,g5)
    c: Coincident(g5,g6)
    c: Horizontal(g6)
    c: Coincident(g6,g7)
    c: Coincident(g7,g8)
    c: Coincident(g8,g3)
    c: Horizontal(g9)
    c: Coincident(g9,g10)
    c: Coincident(g10,g11)
    c: Coincident(g12,g13)
    c: Coincident(g13,g9)
    c: Horizontal(g14)
    c: Coincident(g14,g15)
    c: Coincident(g15,g16)
    c: Coincident(g16,g17)
    c: Horizontal(g17)
    c: Coincident(g17,g18)
    c: Coincident(g19,g14)
    c: Horizontal(g20)
    c: Coincident(g20,g21)
    c: Coincident(g21,g22)
    c: Coincident(g22,g23)
    c: Horizontal(g23)
    c: Coincident(g23,g24)
    c: Coincident(g24,g25)
    c: Coincident(g25,g20)
    c: Horizontal(g26)
    c: Coincident(g26,g27)
    c: Coincident(g27,g28)
    c: Coincident(g28,g29)
    c: Horizontal(g29)
    c: Coincident(g29,g30)
    c: Coincident(g30,g31)
    c: Coincident(g31,g26)
    c: Horizontal(g32)
    c: Coincident(g32,g33)
    c: Coincident(g33,g34)
    c: Coincident(g34,g35)
    c: Horizontal(g35)
    c: Coincident(g35,g36)
    c: Coincident(g36,g37)
    c: Coincident(g37,g32)
    c: Horizontal(g38)
    c: Coincident(g38,g39)
    c: Coincident(g39,g40)
    c: Coincident(g40,g41)
    c: Horizontal(g41)
    c: Coincident(g41,g42)
    c: Coincident(g43,g38)
    c: Horizontal(g44)
    c: Coincident(g44,g45)
    c: Coincident(g45,g46)
    c: Coincident(g46,g47)
    c: Horizontal(g47)
    c: Coincident(g47,g48)
    c: Coincident(g48,g49)
    c: Coincident(g49,g44)
    c: Horizontal(g50)
    c: Coincident(g50,g51)
    c: Coincident(g51,g52)
    c: Coincident(g52,g53)
    c: Horizontal(g53)
    c: Coincident(g53,g54)
    c: Coincident(g54,g55)
    c: Coincident(g55,g50)
    c: Horizontal(g56)
    c: Coincident(g56,g57)
    c: Coincident(g57,g58)
    c: Coincident(g58,g59)
    c: Horizontal(g59)
    c: Coincident(g59,g60)
    c: Coincident(g60,g61)
    c: Coincident(g61,g56)
    c: Horizontal(g62)
    c: Coincident(g62,g63)
    c: Coincident(g63,g64)
    c: Coincident(g64,g65)
    c: Horizontal(g65)
    c: Coincident(g65,g66)
    c: Coincident(g67,g62)
    c: Horizontal(g68)
    c: Coincident(g68,g69)
    c: Coincident(g69,g70)
    c: Coincident(g70,g71)
    c: Horizontal(g71)
    c: Coincident(g71,g72)
    c: Coincident(g72,g73)
    c: Coincident(g73,g68)
    c: Horizontal(g74)
    c: Coincident(g74,g75)
    c: Coincident(g75,g76)
    c: Coincident(g76,g77)
    c: Horizontal(g77)
    c: Coincident(g77,g78)
    c: Coincident(g78,g79)
    c: Coincident(g79,g74)
    c: Horizontal(g80)
    c: Coincident(g80,g81)
    c: Coincident(g81,g82)
    c: Coincident(g82,g83)
    c: Horizontal(g83)
    c: Coincident(g83,g84)
    c: Coincident(g84,g85)
    c: Coincident(g85,g80)
    c: Horizontal(g86)
    c: Coincident(g86,g87)
    c: Coincident(g87,g88)
    c: Coincident(g88,g89)
    c: Horizontal(g89)
    c: Coincident(g89,g90)
    c: Coincident(g91,g86)
    c: Horizontal(g92)
    c: Coincident(g92,g93)
    c: Coincident(g93,g94)
    c: Coincident(g94,g95)
    c: Horizontal(g95)
    c: Coincident(g95,g96)
    c: Coincident(g96,g97)
    c: Coincident(g97,g92)
    c: Horizontal(g98)
    c: Coincident(g98,g99)
    c: Coincident(g99,g100)
    c: Coincident(g100,g101)
    c: Horizontal(g101)
    c: Coincident(g101,g102)
    c: Coincident(g102,g103)
    c: Coincident(g103,g98)
    c: Horizontal(g104)
    c: Coincident(g104,g105)
    c: Coincident(g105,g106)
    c: Coincident(g106,g107)
    c: Horizontal(g107)
    c: Coincident(g107,g108)
    c: Coincident(g108,g109)
    c: Coincident(g109,g104)
    c: Horizontal(g110)
    c: Coincident(g110,g111)
    c: Coincident(g111,g112)
    c: Coincident(g112,g113)
    c: Horizontal(g113)
    c: Coincident(g113,g114)
    c: Coincident(g115,g110)
    c: Horizontal(g116)
    c: Coincident(g116,g117)
    c: Coincident(g117,g118)
    c: Coincident(g118,g119)
    c: Horizontal(g119)
    c: Coincident(g119,g120)
    c: Coincident(g120,g121)
    c: Coincident(g121,g116)
    c: Horizontal(g122)
    c: Coincident(g122,g123)
    c: Coincident(g123,g124)
    c: Coincident(g124,g125)
    c: Horizontal(g125)
    c: Coincident(g125,g126)
    c: Coincident(g126,g127)
    c: Coincident(g127,g122)
    c: Horizontal(g128)
    c: Coincident(g128,g129)
    c: Coincident(g129,g130)
    c: Coincident(g130,g131)
    c: Horizontal(g131)
    c: Coincident(g131,g132)
    c: Coincident(g132,g133)
    c: Coincident(g133,g128)
    c: Horizontal(g134)
    c: Coincident(g134,g135)
    c: Coincident(g135,g136)
    c: Coincident(g136,g137)
    c: Horizontal(g137)
    c: Coincident(g137,g138)
    c: Coincident(g139,g134)
    c: Horizontal(g140)
    c: Coincident(g140,g141)
    c: Coincident(g141,g142)
    c: Coincident(g142,g143)
    c: Horizontal(g143)
    c: Coincident(g143,g144)
    c: Coincident(g144,g145)
    c: Coincident(g145,g140)
    c: Horizontal(g146)
    c: Coincident(g146,g147)
    c: Coincident(g147,g148)
    c: Coincident(g148,g149)
    c: Horizontal(g149)
    c: Coincident(g149,g150)
    c: Coincident(g150,g151)
    c: Coincident(g151,g146)
    c: Horizontal(g152)
    c: Coincident(g152,g153)
    c: Coincident(g153,g154)
    c: Coincident(g154,g155)
    c: Horizontal(g155)
    c: Coincident(g155,g156)
    c: Coincident(g156,g157)
    c: Coincident(g157,g152)
    c: Horizontal(g158)
    c: Coincident(g158,g159)
    c: Coincident(g159,g160)
    c: Coincident(g160,g161)
    c: Horizontal(g161)
    c: Coincident(g161,g162)
    c: Coincident(g163,g158)
    c: Horizontal(g164)
    c: Coincident(g164,g165)
    c: Coincident(g165,g166)
    c: Coincident(g166,g167)
    c: Horizontal(g167)
    c: Coincident(g167,g168)
    c: Coincident(g168,g169)
    c: Coincident(g169,g164)
    c: Horizontal(g170)
    c: Coincident(g170,g171)
    c: Coincident(g171,g172)
    c: Coincident(g172,g173)
    c: Horizontal(g173)
    c: Coincident(g173,g174)
    c: Coincident(g174,g175)
    c: Coincident(g175,g170)
    c: Horizontal(g176)
    c: Coincident(g176,g177)
    c: Coincident(g177,g178)
    c: Coincident(g178,g179)
    c: Horizontal(g179)
    c: Coincident(g179,g180)
    c: Coincident(g180,g181)
    c: Coincident(g181,g176)
    c: Horizontal(g182)
    c: Coincident(g182,g183)
    c: Coincident(g183,g184)
    c: Coincident(g184,g185)
    c: Horizontal(g185)
    c: Coincident(g185,g186)
    c: Coincident(g187,g182)
    c: Horizontal(g188)
    c: Coincident(g188,g189)
    c: Coincident(g189,g190)
    c: Coincident(g190,g191)
    c: Horizontal(g191)
    c: Coincident(g191,g192)
    c: Coincident(g192,g193)
    c: Coincident(g193,g188)
    c: Horizontal(g194)
    c: Coincident(g194,g195)
    c: Coincident(g195,g196)
    c: Coincident(g196,g197)
    c: Horizontal(g197)
    c: Coincident(g197,g198)
    c: Coincident(g198,g199)
    c: Coincident(g199,g194)
    c: Horizontal(g200)
    c: Coincident(g200,g201)
    c: Coincident(g201,g202)
    c: Coincident(g202,g203)
    c: Horizontal(g203)
    c: Coincident(g203,g204)
    c: Coincident(g204,g205)
    c: Coincident(g205,g200)
    c: Horizontal(g206)
    c: Coincident(g206,g207)
    c: Coincident(g207,g208)
    c: Coincident(g208,g209)
    c: Horizontal(g209)
    c: Coincident(g209,g210)
    c: Coincident(g211,g206)
    c: Horizontal(g212)
    c: Coincident(g212,g213)
    c: Coincident(g213,g214)
    c: Coincident(g214,g215)
    c: Horizontal(g215)
    c: Coincident(g215,g216)
    c: Coincident(g216,g217)
    c: Coincident(g217,g212)
    c: Horizontal(g218)
    c: Coincident(g218,g219)
    c: Coincident(g219,g220)
    c: Coincident(g220,g221)
    c: Horizontal(g221)
    c: Coincident(g221,g222)
    c: Coincident(g222,g223)
    c: Coincident(g223,g218)
    c: Horizontal(g224)
    c: Coincident(g224,g225)
    c: Coincident(g225,g226)
    c: Coincident(g226,g227)
    c: Horizontal(g227)
    c: Coincident(g227,g228)
    c: Coincident(g228,g229)
    c: Coincident(g229,g224)
    c: Horizontal(g230)
    c: Coincident(g230,g231)
    c: Coincident(g231,g232)
    c: Coincident(g232,g233)
    c: Horizontal(g233)
    c: Coincident(g233,g234)
    c: Horizontal(g235)
    c: Coincident(g235,g236)
    c: Coincident(g236,g237)
    c: Coincident(g237,g238)
    c: Horizontal(g238)
    c: Coincident(g238,g239)
    c: Coincident(g239,g240)
    c: Coincident(g240,g235)
    c: Coincident(g241,g242)
    c: Horizontal(g242)
    c: Coincident(g242,g243)
    c: Coincident(g243,g244)
    c: Horizontal(g245)
    c: Coincident(g245,g246)
    c: Coincident(g246,g247)
    c: Coincident(g247,g248)
    c: Horizontal(g248)
    c: Coincident(g248,g249)
    c: Coincident(g249,g250)
    c: Coincident(g250,g245)
    c: Coincident(g251,g252)
    c: Horizontal(g252)
    c: Coincident(g252,g253)
    c: Vertical(g255)
    c: Coincident(g256,g244)
    c: Coincident(g254,g244)
    c: Coincident(g267,g241)
    c: Coincident(g267,g256)
    c: Coincident(g268,g230)
    c: Coincident(g268,g255)
    c: Coincident(g234,g255)
    c: Coincident(g211,g258)
    c: Coincident(g210,g258)
    c: Coincident(g187,g259)
    c: Coincident(g186,g259)
    c: Coincident(g163,g260)
    c: Coincident(g162,g260)
    c: Coincident(g139,g261)
    c: Coincident(g138,g261)
    c: Coincident(g115,g262)
    c: Coincident(g114,g262)
    c: Coincident(g91,g263)
    c: Coincident(g90,g263)
    c: Coincident(g67,g264)
    c: Coincident(g66,g264)
    c: Coincident(g43,g265)
    c: Coincident(g42,g265)
    c: Coincident(g19,g266)
    c: Coincident(g18,g266)
    c: Coincident(g269,g11)
    c: Coincident(g269,g12)
    c: Horizontal(g269)
    c: Coincident(g271,g270)
    c: Coincident(g271,g1)
    c: Horizontal(g271)
    c: Coincident(g272,g270)
    c: Coincident(g272,g0)
    c: Coincident(g273,g251)
    c: Coincident(g273,g257)
    c: Coincident(g274,g257)
    c: Coincident(g274,g253)
FEATURE [Part::Extrusion] Extrude002
  Base = -> Sketch011
  Dir = (1,0,2e-16)
  DirMode = 2
  FaceMakerClass = Part::FaceMakerBullseye
  FaceMakerMode = 3
  LengthFwd = 10
  LengthRev = 0
  Placement = pos=(-6,0,0) rot=(0,0,1;0rad)
  Solid = true
  Symmetric = false
FEATURE [Sketcher::SketchObject] Sketch012
  ArcFitTolerance = 1e-06
  FullyConstrained = false
  MakeInternals = false
  MapMode = 5
  Placement = pos=(1e-16,-54.9444,2.06e-14) rot=(1,0,0;1.5708rad)
  sketch-geometry (37):
    g0: LineSegment StartX=10.2322 StartY=9.97629 StartZ=0 EndX=10.2322 EndY=14.9763 EndZ=0
    g1: LineSegment StartX=10.2322 StartY=14.9763 StartZ=0 EndX=5.90209 EndY=17.4763 EndZ=0
    g2: LineSegment StartX=5.90209 StartY=17.4763 StartZ=0 EndX=1.57196 EndY=14.9763 EndZ=0
    g3: LineSegment StartX=1.57196 StartY=14.9763 StartZ=0 EndX=1.57196 EndY=9.97629 EndZ=0
    g4: LineSegment StartX=1.57196 StartY=9.97629 StartZ=0 EndX=5.90209 EndY=7.47629 EndZ=0
    g5: LineSegment StartX=5.90209 StartY=7.47629 StartZ=0 EndX=10.2322 EndY=9.97629 EndZ=0
    g6: Circle [constr] CenterX=5.90209 CenterY=12.4763 CenterZ=0 NormalX=0 NormalY=0 NormalZ=1 AngleXU=0 Radius=5
    g7: LineSegment StartX=15.0623 StartY=1.61026 StartZ=0 EndX=15.0623 EndY=6.61026 EndZ=0
    g8: LineSegment StartX=15.0623 StartY=6.61026 StartZ=0 EndX=10.7322 EndY=9.11026 EndZ=0
    g9: LineSegment StartX=10.7322 StartY=9.11026 StartZ=0 EndX=6.40209 EndY=6.61026 EndZ=0
    g10: LineSegment StartX=6.40209 StartY=6.61026 StartZ=0 EndX=6.40209 EndY=1.61026 EndZ=0
    g11: LineSegment StartX=6.40209 StartY=1.61026 StartZ=0 EndX=10.7322 EndY=-0.889736 EndZ=0
    g12: LineSegment StartX=10.7322 StartY=-0.889736 StartZ=0 EndX=15.0623 EndY=1.61026 EndZ=0
    g13: Circle [constr] CenterX=10.7322 CenterY=4.11026 CenterZ=0 NormalX=0 NormalY=0 NormalZ=1 AngleXU=0 Radius=5
    g14: LineSegment [constr] StartX=10.2322 StartY=9.97629 StartZ=0 EndX=11.2322 EndY=9.97629 EndZ=0
    g15: LineSegment [constr] StartX=11.2322 StartY=9.97629 StartZ=0 EndX=10.7322 EndY=9.11026 EndZ=0
    g16: LineSegment [constr] StartX=10.7322 StartY=9.11026 StartZ=0 EndX=10.2322 EndY=9.97629 EndZ=0
    g17: LineSegment [constr] StartX=6.40209 StartY=1.61026 StartZ=0 EndX=5.40209 EndY=1.61026 EndZ=0
    g18: LineSegment [constr] StartX=5.40209 StartY=1.61026 StartZ=0 EndX=5.90209 EndY=0.744239 EndZ=0
    g19: LineSegment [constr] StartX=5.90209 StartY=0.744239 StartZ=0 EndX=6.40209 EndY=1.61026 EndZ=0
    g20: LineSegment StartX=10.2322 StartY=-6.75576 StartZ=0 EndX=10.2322 EndY=-1.75576 EndZ=0
    g21: LineSegment StartX=10.2322 StartY=-1.75576 StartZ=0 EndX=5.90209 EndY=0.744239 EndZ=0
    g22: LineSegment StartX=5.90209 StartY=0.744239 StartZ=0 EndX=1.57196 EndY=-1.75576 EndZ=0
    g23: LineSegment StartX=1.57196 StartY=-1.75576 StartZ=0 EndX=1.57196 EndY=-6.75576 EndZ=0
    g24: LineSegment StartX=1.57196 StartY=-6.75576 StartZ=0 EndX=5.90209 EndY=-9.25576 EndZ=0
    g25: LineSegment StartX=5.90209 StartY=-9.25576 StartZ=0 EndX=10.2322 EndY=-6.75576 EndZ=0
    g26: Circle [constr] CenterX=5.90209 CenterY=-4.25576 CenterZ=0 NormalX=0 NormalY=0 NormalZ=1 AngleXU=0 Radius=5
    g27: LineSegment [constr] StartX=10.2322 StartY=-6.75576 StartZ=0 EndX=11.2322 EndY=-6.75576 EndZ=0
    g28: LineSegment [constr] StartX=11.2322 StartY=-6.75576 StartZ=0 EndX=10.7322 EndY=-7.62179 EndZ=0
    g29: LineSegment [constr] StartX=10.7322 StartY=-7.62179 StartZ=0 EndX=10.2322 EndY=-6.75576 EndZ=0
    g30: LineSegment StartX=15.0623 StartY=-15.1218 StartZ=0 EndX=15.0623 EndY=-10.1218 EndZ=0
    g31: LineSegment StartX=15.0623 StartY=-10.1218 StartZ=0 EndX=10.7322 EndY=-7.62179 EndZ=0
    g32: LineSegment StartX=10.7322 StartY=-7.62179 StartZ=0 EndX=6.40209 EndY=-10.1218 EndZ=0
    g33: LineSegment StartX=6.40209 StartY=-10.1218 StartZ=0 EndX=6.40209 EndY=-15.1218 EndZ=0
    g34: LineSegment StartX=6.40209 StartY=-15.1218 StartZ=0 EndX=10.7322 EndY=-17.6218 EndZ=0
    g35: LineSegment StartX=10.7322 StartY=-17.6218 StartZ=0 EndX=15.0623 EndY=-15.1218 EndZ=0
    g36: Circle [constr] CenterX=10.7322 CenterY=-12.6218 CenterZ=0 NormalX=0 NormalY=0 NormalZ=1 AngleXU=0 Radius=5
  constraints (87):
    c: Coincident(g0,g1)
    c: Coincident(g1,g2)
    c: Coincident(g2,g3)
    c: Coincident(g3,g4)
    c: Coincident(g4,g5)
    c: Coincident(g5,g0)
    c: Equal(g0, g1-g5) x5
    c: PointOnObject(g0,g6)
    c: PointOnObject(g1,g6)
    c: PointOnObject(g2,g6)
    c: PointOnObject(g3,g6)
    c: PointOnObject(g4,g6)
    c: PointOnObject(g5,g6)
    c: Diameter(g6) = 10
    c: Vertical(g0)
    c: Coincident(g7,g8)
    c: Coincident(g8,g9)
    c: Coincident(g9,g10)
    c: Coincident(g10,g11)
    c: Coincident(g11,g12)
    c: Coincident(g12,g7)
    c: Equal(g7, g8-g12) x5
    c: PointOnObject(g7,g13)
    c: PointOnObject(g8,g13)
    c: PointOnObject(g9,g13)
    c: PointOnObject(g10,g13)
    c: PointOnObject(g11,g13)
    c: PointOnObject(g12,g13)
    c: Vertical(g10)
    c: Equal(g13,g6)
    c: Coincident(g0,g14)
    c: Coincident(g14,g15)
    c: Coincident(g15,g16)
    c: Coincident(g16,g14)
    c: Equal(g15,g16)
    c: Equal(g16,g14)
    c: Horizontal(g14)
    c: Distance(g14) = 1
    c: Coincident(g8,g15)
    c: Coincident(g10,g17)
    c: Horizontal(g17)
    c: Coincident(g17,g18)
    c: Coincident(g18,g19)
    c: Coincident(g19,g17)
    c: Equal(g17,g18)
    c: Equal(g18,g19)
    c: Distance(g17) = 1
    c: Coincident(g20,g21)
    c: Coincident(g21,g22)
    c: Coincident(g22,g23)
    c: Coincident(g23,g24)
    c: Coincident(g24,g25)
    c: Coincident(g25,g20)
    c: Equal(g20, g21-g25) x5
    c: PointOnObject(g20,g26)
    c: PointOnObject(g21,g26)
    c: PointOnObject(g22,g26)
    c: PointOnObject(g23,g26)
    c: PointOnObject(g24,g26)
    c: PointOnObject(g25,g26)
    c: Vertical(g23)
    c: Equal(g26,g13)
    c: Coincident(g21,g18)
    c: Coincident(g20,g27)
    c: Horizontal(g27)
    c: Coincident(g27,g28)
    c: Coincident(g28,g29)
    c: Coincident(g29,g27)
    c: Equal(g27,g29)
    c: Equal(g29,g28)
    c: Distance(g27) = 1
    c: Coincident(g30,g31)
    c: Coincident(g31,g32)
    c: Coincident(g32,g33)
    c: Coincident(g33,g34)
    c: Coincident(g34,g35)
    c: Coincident(g35,g30)
    c: Equal(g30, g31-g35) x5
    c: PointOnObject(g30,g36)
    c: PointOnObject(g31,g36)
    c: PointOnObject(g32,g36)
    c: PointOnObject(g33,g36)
    c: PointOnObject(g34,g36)
    c: PointOnObject(g35,g36)
    c: Vertical(g33)
    c: Equal(g36,g26)
    c: Coincident(g31,g28)
FEATURE [Sketcher::SketchObject] Sketch013
  ArcFitTolerance = 1e-06
  FullyConstrained = false
  MakeInternals = false
  Placement = pos=(0,-54.9444,0) rot=(1,0,0;1.5708rad)
  sketch-geometry (374):
    g0: LineSegment StartX=10.2322 StartY=9.97629 StartZ=0 EndX=10.2322 EndY=14.9763 EndZ=0
    g1: LineSegment StartX=10.2322 StartY=14.9763 StartZ=0 EndX=10.2322 EndY=14.9763 EndZ=0
    g2: LineSegment StartX=1.57196 StartY=14.9763 StartZ=0 EndX=1.57196 EndY=14.9763 EndZ=0
    g3: LineSegment StartX=1.57196 StartY=9.97629 StartZ=0 EndX=1.57196 EndY=9.97629 EndZ=0
    g4: LineSegment StartX=5.90209 StartY=7.47629 StartZ=0 EndX=10.2322 EndY=9.97629 EndZ=0
    g5: LineSegment StartX=15.0623 StartY=1.61026 StartZ=0 EndX=15.0623 EndY=6.61026 EndZ=0
    g6: LineSegment StartX=15.0623 StartY=6.61026 StartZ=0 EndX=10.7322 EndY=9.11026 EndZ=0
    g7: LineSegment StartX=10.7322 StartY=9.11026 StartZ=0 EndX=6.40209 EndY=6.61026 EndZ=0
    g8: LineSegment StartX=6.40209 StartY=6.61026 StartZ=0 EndX=6.40209 EndY=1.61026 EndZ=0
    g9: LineSegment StartX=6.40209 StartY=1.61026 StartZ=0 EndX=10.7322 EndY=-0.889736 EndZ=0
    g10: LineSegment StartX=10.7322 StartY=-0.889736 StartZ=0 EndX=15.0623 EndY=1.61026 EndZ=0
    g11: LineSegment StartX=10.2322 StartY=-6.75576 StartZ=0 EndX=10.2322 EndY=-1.75576 EndZ=0
    g12: LineSegment StartX=10.2322 StartY=-1.75576 StartZ=0 EndX=5.90209 EndY=0.744239 EndZ=0
    g13: LineSegment StartX=5.90209 StartY=0.744239 StartZ=0 EndX=1.57196 EndY=-1.75576 EndZ=0
    g14: LineSegment StartX=1.57196 StartY=-1.75576 StartZ=0 EndX=1.57196 EndY=-6.75576 EndZ=0
    g15: LineSegment StartX=1.57196 StartY=-6.75576 StartZ=0 EndX=5.90209 EndY=-9.25576 EndZ=0
    g16: LineSegment StartX=5.90209 StartY=-9.25576 StartZ=0 EndX=10.2322 EndY=-6.75576 EndZ=0
    g17: LineSegment StartX=15.0623 StartY=-13.7374 StartZ=0 EndX=15.0623 EndY=-10.1218 EndZ=0
    g18: LineSegment StartX=15.0623 StartY=-10.1218 StartZ=0 EndX=10.7322 EndY=-7.62179 EndZ=0
    g19: LineSegment StartX=10.7322 StartY=-7.62179 StartZ=0 EndX=6.40209 EndY=-10.1218 EndZ=0
    g20: LineSegment StartX=6.40209 StartY=-10.1218 StartZ=0 EndX=6.40209 EndY=-13.7374 EndZ=0
    g21: LineSegment StartX=19.7322 StartY=9.97629 StartZ=0 EndX=19.7322 EndY=14.9763 EndZ=0
    g22: LineSegment StartX=19.7322 StartY=14.9763 StartZ=0 EndX=19.7322 EndY=14.9763 EndZ=0
    g23: LineSegment StartX=11.072 StartY=14.9763 StartZ=0 EndX=11.072 EndY=14.9763 EndZ=0
    g24: LineSegment StartX=11.072 StartY=14.9763 StartZ=0 EndX=11.072 EndY=9.97629 EndZ=0
    g25: LineSegment StartX=11.072 StartY=9.97629 StartZ=0 EndX=15.4021 EndY=7.47629 EndZ=0
    g26: LineSegment StartX=15.4021 StartY=7.47629 StartZ=0 EndX=19.7322 EndY=9.97629 EndZ=0
    g27: LineSegment StartX=24.5623 StartY=1.61026 StartZ=0 EndX=24.5623 EndY=6.61026 EndZ=0
    g28: LineSegment StartX=24.5623 StartY=6.61026 StartZ=0 EndX=20.2322 EndY=9.11026 EndZ=0
    g29: LineSegment StartX=20.2322 StartY=9.11026 StartZ=0 EndX=15.9021 EndY=6.61026 EndZ=0
    g30: LineSegment StartX=15.9021 StartY=6.61026 StartZ=0 EndX=15.9021 EndY=1.61026 EndZ=0
    g31: LineSegment StartX=15.9021 StartY=1.61026 StartZ=0 EndX=20.2322 EndY=-0.889736 EndZ=0
    g32: LineSegment StartX=20.2322 StartY=-0.889736 StartZ=0 EndX=24.5623 EndY=1.61026 EndZ=0
    g33: LineSegment StartX=19.7322 StartY=-6.75576 StartZ=0 EndX=19.7322 EndY=-1.75576 EndZ=0
    g34: LineSegment StartX=15.4021 StartY=0.744239 StartZ=0 EndX=11.072 EndY=-1.75576 EndZ=0
    g35: LineSegment StartX=11.072 StartY=-1.75576 StartZ=0 EndX=11.072 EndY=-6.75576 EndZ=0
    g36: LineSegment StartX=11.072 StartY=-6.75576 StartZ=0 EndX=15.4021 EndY=-9.25576 EndZ=0
    g37: LineSegment StartX=15.4021 StartY=-9.25576 StartZ=0 EndX=19.7322 EndY=-6.75576 EndZ=0
    g38: LineSegment StartX=24.5623 StartY=-13.7374 StartZ=0 EndX=24.5623 EndY=-10.1218 EndZ=0
    g39: LineSegment StartX=24.5623 StartY=-10.1218 StartZ=0 EndX=20.2322 EndY=-7.62179 EndZ=0
    g40: LineSegment StartX=20.2322 StartY=-7.62179 StartZ=0 EndX=15.9021 EndY=-10.1218 EndZ=0
    g41: LineSegment StartX=15.9021 StartY=-10.1218 StartZ=0 EndX=15.9021 EndY=-13.7374 EndZ=0
    g42: LineSegment StartX=29.2322 StartY=9.97629 StartZ=0 EndX=29.2322 EndY=14.9763 EndZ=0
    g43: LineSegment StartX=29.2322 StartY=14.9763 StartZ=0 EndX=29.2322 EndY=14.9763 EndZ=0
    g44: LineSegment StartX=20.572 StartY=14.9763 StartZ=0 EndX=20.572 EndY=14.9763 EndZ=0
    g45: LineSegment StartX=20.572 StartY=14.9763 StartZ=0 EndX=20.572 EndY=9.97629 EndZ=0
    g46: LineSegment StartX=20.572 StartY=9.97629 StartZ=0 EndX=24.9021 EndY=7.47629 EndZ=0
    g47: LineSegment StartX=24.9021 StartY=7.47629 StartZ=0 EndX=29.2322 EndY=9.97629 EndZ=0
    g48: LineSegment StartX=34.0623 StartY=1.61026 StartZ=0 EndX=34.0623 EndY=6.61026 EndZ=0
    g49: LineSegment StartX=34.0623 StartY=6.61026 StartZ=0 EndX=29.7322 EndY=9.11026 EndZ=0
    g50: LineSegment StartX=29.7322 StartY=9.11026 StartZ=0 EndX=25.4021 EndY=6.61026 EndZ=0
    g51: LineSegment StartX=25.4021 StartY=6.61026 StartZ=0 EndX=25.4021 EndY=1.61026 EndZ=0
    g52: LineSegment StartX=25.4021 StartY=1.61026 StartZ=0 EndX=29.7322 EndY=-0.889736 EndZ=0
    g53: LineSegment StartX=29.7322 StartY=-0.889736 StartZ=0 EndX=34.0623 EndY=1.61026 EndZ=0
    g54: LineSegment StartX=29.2322 StartY=-6.75576 StartZ=0 EndX=29.2322 EndY=-1.75576 EndZ=0
    g55: LineSegment StartX=29.2322 StartY=-1.75576 StartZ=0 EndX=24.9021 EndY=0.744239 EndZ=0
    g56: LineSegment StartX=24.9021 StartY=0.744239 StartZ=0 EndX=20.572 EndY=-1.75576 EndZ=0
    g57: LineSegment StartX=20.572 StartY=-1.75576 StartZ=0 EndX=20.572 EndY=-6.75576 EndZ=0
    g58: LineSegment StartX=20.572 StartY=-6.75576 StartZ=0 EndX=24.9021 EndY=-9.25576 EndZ=0
    g59: LineSegment StartX=24.9021 StartY=-9.25576 StartZ=0 EndX=29.2322 EndY=-6.75576 EndZ=0
    g60: LineSegment StartX=34.0623 StartY=-13.7374 StartZ=0 EndX=34.0623 EndY=-10.1218 EndZ=0
    g61: LineSegment StartX=34.0623 StartY=-10.1218 StartZ=0 EndX=29.7322 EndY=-7.62179 EndZ=0
    g62: LineSegment StartX=29.7322 StartY=-7.62179 StartZ=0 EndX=25.4021 EndY=-10.1218 EndZ=0
    g63: LineSegment StartX=25.4021 StartY=-10.1218 StartZ=0 EndX=25.4021 EndY=-13.7374 EndZ=0
    g64: LineSegment StartX=38.7322 StartY=9.97629 StartZ=0 EndX=38.7322 EndY=14.9763 EndZ=0
    g65: LineSegment StartX=38.7322 StartY=14.9763 StartZ=0 EndX=38.7322 EndY=14.9763 EndZ=0
    g66: LineSegment StartX=30.072 StartY=14.9763 StartZ=0 EndX=30.072 EndY=14.9763 EndZ=0
    g67: LineSegment StartX=30.072 StartY=14.9763 StartZ=0 EndX=30.072 EndY=9.97629 EndZ=0
    g68: LineSegment StartX=30.072 StartY=9.97629 StartZ=0 EndX=34.4021 EndY=7.47629 EndZ=0
    g69: LineSegment StartX=34.4021 StartY=7.47629 StartZ=0 EndX=38.7322 EndY=9.97629 EndZ=0
    g70: LineSegment StartX=43.5623 StartY=1.61026 StartZ=0 EndX=43.5623 EndY=6.61026 EndZ=0
    g71: LineSegment StartX=43.5623 StartY=6.61026 StartZ=0 EndX=39.2322 EndY=9.11026 EndZ=0
    g72: LineSegment StartX=39.2322 StartY=9.11026 StartZ=0 EndX=34.9021 EndY=6.61026 EndZ=0
    g73: LineSegment StartX=34.9021 StartY=6.61026 StartZ=0 EndX=34.9021 EndY=1.61026 EndZ=0
    g74: LineSegment StartX=34.9021 StartY=1.61026 StartZ=0 EndX=39.2322 EndY=-0.889736 EndZ=0
    g75: LineSegment StartX=39.2322 StartY=-0.889736 StartZ=0 EndX=43.5623 EndY=1.61026 EndZ=0
    g76: LineSegment StartX=38.7322 StartY=-6.75576 StartZ=0 EndX=38.7322 EndY=-1.75576 EndZ=0
    g77: LineSegment StartX=38.7322 StartY=-1.75576 StartZ=0 EndX=34.4021 EndY=0.744239 EndZ=0
    g78: LineSegment StartX=34.4021 StartY=0.744239 StartZ=0 EndX=30.072 EndY=-1.75576 EndZ=0
    g79: LineSegment StartX=30.072 StartY=-1.75576 StartZ=0 EndX=30.072 EndY=-6.75576 EndZ=0
    g80: LineSegment StartX=30.072 StartY=-6.75576 StartZ=0 EndX=34.4021 EndY=-9.25576 EndZ=0
    g81: LineSegment StartX=34.4021 StartY=-9.25576 StartZ=0 EndX=38.7322 EndY=-6.75576 EndZ=0
    g82: LineSegment StartX=43.5623 StartY=-13.7374 StartZ=0 EndX=43.5623 EndY=-10.1218 EndZ=0
    g83: LineSegment StartX=43.5623 StartY=-10.1218 StartZ=0 EndX=39.2322 EndY=-7.62179 EndZ=0
    g84: LineSegment StartX=39.2322 StartY=-7.62179 StartZ=0 EndX=34.9021 EndY=-10.1218 EndZ=0
    g85: LineSegment StartX=34.9021 StartY=-10.1218 StartZ=0 EndX=34.9021 EndY=-13.7374 EndZ=0
    g86: LineSegment StartX=48.2322 StartY=9.97629 StartZ=0 EndX=48.2322 EndY=14.9763 EndZ=0
    g87: LineSegment StartX=48.2322 StartY=14.9763 StartZ=0 EndX=48.2322 EndY=14.9763 EndZ=0
    g88: LineSegment StartX=39.572 StartY=14.9763 StartZ=0 EndX=39.572 EndY=14.9763 EndZ=0
    g89: LineSegment StartX=39.572 StartY=14.9763 StartZ=0 EndX=39.572 EndY=9.97629 EndZ=0
    g90: LineSegment StartX=39.572 StartY=9.97629 StartZ=0 EndX=43.9021 EndY=7.47629 EndZ=0
    g91: LineSegment StartX=43.9021 StartY=7.47629 StartZ=0 EndX=48.2322 EndY=9.97629 EndZ=0
    g92: LineSegment StartX=53.0623 StartY=1.61026 StartZ=0 EndX=53.0623 EndY=6.61026 EndZ=0
    g93: LineSegment StartX=53.0623 StartY=6.61026 StartZ=0 EndX=48.7322 EndY=9.11026 EndZ=0
    g94: LineSegment StartX=48.7322 StartY=9.11026 StartZ=0 EndX=44.4021 EndY=6.61026 EndZ=0
    g95: LineSegment StartX=44.4021 StartY=6.61026 StartZ=0 EndX=44.4021 EndY=1.61026 EndZ=0
    g96: LineSegment StartX=44.4021 StartY=1.61026 StartZ=0 EndX=48.7322 EndY=-0.889736 EndZ=0
    g97: LineSegment StartX=48.7322 StartY=-0.889736 StartZ=0 EndX=53.0623 EndY=1.61026 EndZ=0
    g98: LineSegment StartX=48.2322 StartY=-6.75576 StartZ=0 EndX=48.2322 EndY=-1.75576 EndZ=0
    g99: LineSegment StartX=48.2322 StartY=-1.75576 StartZ=0 EndX=43.9021 EndY=0.744239 EndZ=0
    g100: LineSegment StartX=43.9021 StartY=0.744239 StartZ=0 EndX=39.572 EndY=-1.75576 EndZ=0
    g101: LineSegment StartX=39.572 StartY=-1.75576 StartZ=0 EndX=39.572 EndY=-6.75576 EndZ=0
    g102: LineSegment StartX=39.572 StartY=-6.75576 StartZ=0 EndX=43.9021 EndY=-9.25576 EndZ=0
    g103: LineSegment StartX=43.9021 StartY=-9.25576 StartZ=0 EndX=48.2322 EndY=-6.75576 EndZ=0
    g104: LineSegment StartX=53.0623 StartY=-13.7374 StartZ=0 EndX=53.0623 EndY=-10.1218 EndZ=0
    g105: LineSegment StartX=53.0623 StartY=-10.1218 StartZ=0 EndX=48.7322 EndY=-7.62179 EndZ=0
    g106: LineSegment StartX=48.7322 StartY=-7.62179 StartZ=0 EndX=44.4021 EndY=-10.1218 EndZ=0
    g107: LineSegment StartX=44.4021 StartY=-10.1218 StartZ=0 EndX=44.4021 EndY=-13.7374 EndZ=0
    g108: LineSegment StartX=57.7322 StartY=9.97629 StartZ=0 EndX=57.7322 EndY=14.9763 EndZ=0
    g109: LineSegment StartX=57.7322 StartY=14.9763 StartZ=0 EndX=57.7322 EndY=14.9763 EndZ=0
    g110: LineSegment StartX=49.072 StartY=14.9763 StartZ=0 EndX=49.072 EndY=14.9763 EndZ=0
    g111: LineSegment StartX=49.072 StartY=14.9763 StartZ=0 EndX=49.072 EndY=9.97629 EndZ=0
    g112: LineSegment StartX=49.072 StartY=9.97629 StartZ=0 EndX=53.4021 EndY=7.47629 EndZ=0
    g113: LineSegment StartX=53.4021 StartY=7.47629 StartZ=0 EndX=57.7322 EndY=9.97629 EndZ=0
    g114: LineSegment StartX=62.5623 StartY=1.61026 StartZ=0 EndX=62.5623 EndY=6.61026 EndZ=0
    g115: LineSegment StartX=62.5623 StartY=6.61026 StartZ=0 EndX=58.2322 EndY=9.11026 EndZ=0
    g116: LineSegment StartX=58.2322 StartY=9.11026 StartZ=0 EndX=53.9021 EndY=6.61026 EndZ=0
    g117: LineSegment StartX=53.9021 StartY=6.61026 StartZ=0 EndX=53.9021 EndY=1.61026 EndZ=0
    g118: LineSegment StartX=53.9021 StartY=1.61026 StartZ=0 EndX=58.2322 EndY=-0.889736 EndZ=0
    g119: LineSegment StartX=58.2322 StartY=-0.889736 StartZ=0 EndX=62.5623 EndY=1.61026 EndZ=0
    g120: LineSegment StartX=57.7322 StartY=-6.75576 StartZ=0 EndX=57.7322 EndY=-1.75576 EndZ=0
    g121: LineSegment StartX=57.7322 StartY=-1.75576 StartZ=0 EndX=53.4021 EndY=0.744239 EndZ=0
    g122: LineSegment StartX=53.4021 StartY=0.744239 StartZ=0 EndX=49.072 EndY=-1.75576 EndZ=0
    g123: LineSegment StartX=49.072 StartY=-1.75576 StartZ=0 EndX=49.072 EndY=-6.75576 EndZ=0
    g124: LineSegment StartX=49.072 StartY=-6.75576 StartZ=0 EndX=53.4021 EndY=-9.25576 EndZ=0
    g125: LineSegment StartX=53.4021 StartY=-9.25576 StartZ=0 EndX=57.7322 EndY=-6.75576 EndZ=0
    g126: LineSegment StartX=62.5623 StartY=-13.7374 StartZ=0 EndX=62.5623 EndY=-10.1218 EndZ=0
    g127: LineSegment StartX=62.5623 StartY=-10.1218 StartZ=0 EndX=58.2322 EndY=-7.62179 EndZ=0
    g128: LineSegment StartX=58.2322 StartY=-7.62179 StartZ=0 EndX=53.9021 EndY=-10.1218 EndZ=0
    g129: LineSegment StartX=53.9021 StartY=-10.1218 StartZ=0 EndX=53.9021 EndY=-13.7374 EndZ=0
    g130: LineSegment StartX=67.2322 StartY=9.97629 StartZ=0 EndX=67.2322 EndY=14.9763 EndZ=0
    g131: LineSegment StartX=67.2322 StartY=14.9763 StartZ=0 EndX=67.2322 EndY=14.9763 EndZ=0
    g132: LineSegment StartX=58.572 StartY=14.9763 StartZ=0 EndX=58.572 EndY=14.9763 EndZ=0
    g133: LineSegment StartX=58.572 StartY=14.9763 StartZ=0 EndX=58.572 EndY=9.97629 EndZ=0
    g134: LineSegment StartX=58.572 StartY=9.97629 StartZ=0 EndX=62.9021 EndY=7.47629 EndZ=0
    g135: LineSegment StartX=62.9021 StartY=7.47629 StartZ=0 EndX=67.2322 EndY=9.97629 EndZ=0
    g136: LineSegment StartX=72.0623 StartY=1.61026 StartZ=0 EndX=72.0623 EndY=6.61026 EndZ=0
    g137: LineSegment StartX=72.0623 StartY=6.61026 StartZ=0 EndX=67.7322 EndY=9.11026 EndZ=0
    g138: LineSegment StartX=67.7322 StartY=9.11026 StartZ=0 EndX=63.4021 EndY=6.61026 EndZ=0
    g139: LineSegment StartX=63.4021 StartY=6.61026 StartZ=0 EndX=63.4021 EndY=1.61026 EndZ=0
    g140: LineSegment StartX=63.4021 StartY=1.61026 StartZ=0 EndX=67.7322 EndY=-0.889736 EndZ=0
    g141: LineSegment StartX=67.7322 StartY=-0.889736 StartZ=0 EndX=72.0623 EndY=1.61026 EndZ=0
    g142: LineSegment StartX=67.2322 StartY=-6.75576 StartZ=0 EndX=67.2322 EndY=-1.75576 EndZ=0
    g143: LineSegment StartX=67.2322 StartY=-1.75576 StartZ=0 EndX=62.9021 EndY=0.744239 EndZ=0
    g144: LineSegment StartX=62.9021 StartY=0.744239 StartZ=0 EndX=58.572 EndY=-1.75576 EndZ=0
    g145: LineSegment StartX=58.572 StartY=-1.75576 StartZ=0 EndX=58.572 EndY=-6.75576 EndZ=0
    g146: LineSegment StartX=58.572 StartY=-6.75576 StartZ=0 EndX=62.9021 EndY=-9.25576 EndZ=0
    g147: LineSegment StartX=62.9021 StartY=-9.25576 StartZ=0 EndX=67.2322 EndY=-6.75576 EndZ=0
    g148: LineSegment StartX=72.0623 StartY=-13.7374 StartZ=0 EndX=72.0623 EndY=-10.1218 EndZ=0
    g149: LineSegment StartX=72.0623 StartY=-10.1218 StartZ=0 EndX=67.7322 EndY=-7.62179 EndZ=0
    g150: LineSegment StartX=67.7322 StartY=-7.62179 StartZ=0 EndX=63.4021 EndY=-10.1218 EndZ=0
    g151: LineSegment StartX=63.4021 StartY=-10.1218 StartZ=0 EndX=63.4021 EndY=-13.7374 EndZ=0
    g152: LineSegment StartX=76.7322 StartY=9.97629 StartZ=0 EndX=76.7322 EndY=14.9763 EndZ=0
    g153: LineSegment StartX=76.7322 StartY=14.9763 StartZ=0 EndX=76.7322 EndY=14.9763 EndZ=0
    g154: LineSegment StartX=68.072 StartY=14.9763 StartZ=0 EndX=68.072 EndY=14.9763 EndZ=0
    g155: LineSegment StartX=68.072 StartY=14.9763 StartZ=0 EndX=68.072 EndY=9.97629 EndZ=0
    g156: LineSegment StartX=68.072 StartY=9.97629 StartZ=0 EndX=72.4021 EndY=7.47629 EndZ=0
    g157: LineSegment StartX=72.4021 StartY=7.47629 StartZ=0 EndX=76.7322 EndY=9.97629 EndZ=0
    g158: LineSegment StartX=81.5623 StartY=1.61026 StartZ=0 EndX=81.5623 EndY=6.61026 EndZ=0
    g159: LineSegment StartX=81.5623 StartY=6.61026 StartZ=0 EndX=77.2322 EndY=9.11026 EndZ=0
    g160: LineSegment StartX=77.2322 StartY=9.11026 StartZ=0 EndX=72.9021 EndY=6.61026 EndZ=0
    g161: LineSegment StartX=72.9021 StartY=6.61026 StartZ=0 EndX=72.9021 EndY=1.61026 EndZ=0
    g162: LineSegment StartX=72.9021 StartY=1.61026 StartZ=0 EndX=77.2322 EndY=-0.889736 EndZ=0
    g163: LineSegment StartX=77.2322 StartY=-0.889736 StartZ=0 EndX=81.5623 EndY=1.61026 EndZ=0
    g164: LineSegment StartX=76.7322 StartY=-6.75576 StartZ=0 EndX=76.7322 EndY=-1.75576 EndZ=0
    g165: LineSegment StartX=76.7322 StartY=-1.75576 StartZ=0 EndX=72.4021 EndY=0.744239 EndZ=0
    g166: LineSegment StartX=72.4021 StartY=0.744239 StartZ=0 EndX=68.072 EndY=-1.75576 EndZ=0
    g167: LineSegment StartX=68.072 StartY=-1.75576 StartZ=0 EndX=68.072 EndY=-6.75576 EndZ=0
    g168: LineSegment StartX=68.072 StartY=-6.75576 StartZ=0 EndX=72.4021 EndY=-9.25576 EndZ=0
    g169: LineSegment StartX=72.4021 StartY=-9.25576 StartZ=0 EndX=76.7322 EndY=-6.75576 EndZ=0
    g170: LineSegment StartX=81.5623 StartY=-13.7374 StartZ=0 EndX=81.5623 EndY=-10.1218 EndZ=0
    g171: LineSegment StartX=81.5623 StartY=-10.1218 StartZ=0 EndX=77.2322 EndY=-7.62179 EndZ=0
    g172: LineSegment StartX=77.2322 StartY=-7.62179 StartZ=0 EndX=72.9021 EndY=-10.1218 EndZ=0
    g173: LineSegment StartX=72.9021 StartY=-10.1218 StartZ=0 EndX=72.9021 EndY=-13.7374 EndZ=0
    g174: LineSegment StartX=86.2322 StartY=9.97629 StartZ=0 EndX=86.2322 EndY=14.9763 EndZ=0
    g175: LineSegment StartX=86.2322 StartY=14.9763 StartZ=0 EndX=86.2322 EndY=14.9763 EndZ=0
    g176: LineSegment StartX=77.572 StartY=14.9763 StartZ=0 EndX=77.572 EndY=14.9763 EndZ=0
    g177: LineSegment StartX=77.572 StartY=14.9763 StartZ=0 EndX=77.572 EndY=9.97629 EndZ=0
    g178: LineSegment StartX=77.572 StartY=9.97629 StartZ=0 EndX=81.9021 EndY=7.47629 EndZ=0
    g179: LineSegment StartX=81.9021 StartY=7.47629 StartZ=0 EndX=86.2322 EndY=9.97629 EndZ=0
    g180: LineSegment StartX=91.0623 StartY=1.61026 StartZ=0 EndX=91.0623 EndY=6.61026 EndZ=0
    g181: LineSegment StartX=91.0623 StartY=6.61026 StartZ=0 EndX=86.7322 EndY=9.11026 EndZ=0
    g182: LineSegment StartX=86.7322 StartY=9.11026 StartZ=0 EndX=82.4021 EndY=6.61026 EndZ=0
    g183: LineSegment StartX=82.4021 StartY=6.61026 StartZ=0 EndX=82.4021 EndY=1.61026 EndZ=0
    g184: LineSegment StartX=82.4021 StartY=1.61026 StartZ=0 EndX=86.7322 EndY=-0.889736 EndZ=0
    g185: LineSegment StartX=86.7322 StartY=-0.889736 StartZ=0 EndX=91.0623 EndY=1.61026 EndZ=0
    g186: LineSegment StartX=86.2322 StartY=-6.75576 StartZ=0 EndX=86.2322 EndY=-1.75576 EndZ=0
    g187: LineSegment StartX=86.2322 StartY=-1.75576 StartZ=0 EndX=81.9021 EndY=0.744239 EndZ=0
    g188: LineSegment StartX=81.9021 StartY=0.744239 StartZ=0 EndX=77.572 EndY=-1.75576 EndZ=0
    g189: LineSegment StartX=77.572 StartY=-1.75576 StartZ=0 EndX=77.572 EndY=-6.75576 EndZ=0
    g190: LineSegment StartX=77.572 StartY=-6.75576 StartZ=0 EndX=81.9021 EndY=-9.25576 EndZ=0
    g191: LineSegment StartX=81.9021 StartY=-9.25576 StartZ=0 EndX=86.2322 EndY=-6.75576 EndZ=0
    g192: LineSegment StartX=91.0623 StartY=-13.7374 StartZ=0 EndX=91.0623 EndY=-10.1218 EndZ=0
    g193: LineSegment StartX=91.0623 StartY=-10.1218 StartZ=0 EndX=86.7322 EndY=-7.62179 EndZ=0
    g194: LineSegment StartX=86.7322 StartY=-7.62179 StartZ=0 EndX=82.4021 EndY=-10.1218 EndZ=0
    g195: LineSegment StartX=82.4021 StartY=-10.1218 StartZ=0 EndX=82.4021 EndY=-13.7374 EndZ=0
    g196: LineSegment StartX=95.7322 StartY=9.97629 StartZ=0 EndX=95.7322 EndY=14.9763 EndZ=0
    g197: LineSegment StartX=95.7322 StartY=14.9763 StartZ=0 EndX=95.7322 EndY=14.9763 EndZ=0
    g198: LineSegment StartX=87.072 StartY=14.9763 StartZ=0 EndX=87.072 EndY=14.9763 EndZ=0
    g199: LineSegment StartX=87.072 StartY=14.9763 StartZ=0 EndX=87.072 EndY=9.97629 EndZ=0
    g200: LineSegment StartX=87.072 StartY=9.97629 StartZ=0 EndX=91.4021 EndY=7.47629 EndZ=0
    g201: LineSegment StartX=91.4021 StartY=7.47629 StartZ=0 EndX=95.7322 EndY=9.97629 EndZ=0
    g202: LineSegment StartX=100.562 StartY=1.61026 StartZ=0 EndX=100.562 EndY=6.61026 EndZ=0
    g203: LineSegment StartX=100.562 StartY=6.61026 StartZ=0 EndX=96.2322 EndY=9.11026 EndZ=0
    g204: LineSegment StartX=96.2322 StartY=9.11026 StartZ=0 EndX=91.9021 EndY=6.61026 EndZ=0
    g205: LineSegment StartX=91.9021 StartY=6.61026 StartZ=0 EndX=91.9021 EndY=1.61026 EndZ=0
    g206: LineSegment StartX=91.9021 StartY=1.61026 StartZ=0 EndX=96.2322 EndY=-0.889736 EndZ=0
    g207: LineSegment StartX=96.2322 StartY=-0.889736 StartZ=0 EndX=100.562 EndY=1.61026 EndZ=0
    g208: LineSegment StartX=95.7322 StartY=-6.75576 StartZ=0 EndX=95.7322 EndY=-1.75576 EndZ=0
    g209: LineSegment StartX=95.7322 StartY=-1.75576 StartZ=0 EndX=91.4021 EndY=0.744239 EndZ=0
    g210: LineSegment StartX=91.4021 StartY=0.744239 StartZ=0 EndX=87.072 EndY=-1.75576 EndZ=0
    g211: LineSegment StartX=87.072 StartY=-1.75576 StartZ=0 EndX=87.072 EndY=-6.75576 EndZ=0
    g212: LineSegment StartX=87.072 StartY=-6.75576 StartZ=0 EndX=91.4021 EndY=-9.25576 EndZ=0
    g213: LineSegment StartX=91.4021 StartY=-9.25576 StartZ=0 EndX=95.7322 EndY=-6.75576 EndZ=0
    g214: LineSegment StartX=100.562 StartY=-13.7374 StartZ=0 EndX=100.562 EndY=-10.1218 EndZ=0
    g215: LineSegment StartX=100.562 StartY=-10.1218 StartZ=0 EndX=96.2322 EndY=-7.62179 EndZ=0
    g216: LineSegment StartX=96.2322 StartY=-7.62179 StartZ=0 EndX=91.9021 EndY=-10.1218 EndZ=0
    g217: LineSegment StartX=91.9021 StartY=-10.1218 StartZ=0 EndX=91.9021 EndY=-13.7374 EndZ=0
    g218: LineSegment StartX=105.232 StartY=9.97629 StartZ=0 EndX=105.232 EndY=14.9763 EndZ=0
    g219: LineSegment StartX=96.572 StartY=14.9763 StartZ=0 EndX=96.572 EndY=14.9763 EndZ=0
    g220: LineSegment StartX=96.572 StartY=9.97629 StartZ=0 EndX=100.902 EndY=7.47629 EndZ=0
    g221: LineSegment StartX=100.902 StartY=7.47629 StartZ=0 EndX=105.232 EndY=9.97629 EndZ=0
    g222: LineSegment StartX=110.062 StartY=1.61026 StartZ=0 EndX=110.062 EndY=6.61026 EndZ=0
    g223: LineSegment StartX=110.062 StartY=6.61026 StartZ=0 EndX=105.732 EndY=9.11026 EndZ=0
    g224: LineSegment StartX=105.732 StartY=9.11026 StartZ=0 EndX=101.402 EndY=6.61026 EndZ=0
    g225: LineSegment StartX=101.402 StartY=6.61026 StartZ=0 EndX=101.402 EndY=1.61026 EndZ=0
    g226: LineSegment StartX=101.402 StartY=1.61026 StartZ=0 EndX=105.732 EndY=-0.889736 EndZ=0
    g227: LineSegment StartX=105.732 StartY=-0.889736 StartZ=0 EndX=110.062 EndY=1.61026 EndZ=0
    g228: LineSegment StartX=105.232 StartY=-6.75576 StartZ=0 EndX=105.232 EndY=-1.75576 EndZ=0
    g229: LineSegment StartX=105.232 StartY=-1.75576 StartZ=0 EndX=100.902 EndY=0.744239 EndZ=0
    g230: LineSegment StartX=100.902 StartY=0.744239 StartZ=0 EndX=96.572 EndY=-1.75576 EndZ=0
    g231: LineSegment StartX=96.572 StartY=-1.75576 StartZ=0 EndX=96.572 EndY=-6.75576 EndZ=0
    g232: LineSegment StartX=96.572 StartY=-6.75576 StartZ=0 EndX=100.902 EndY=-9.25576 EndZ=0
    g233: LineSegment StartX=100.902 StartY=-9.25576 StartZ=0 EndX=105.232 EndY=-6.75576 EndZ=0
    g234: LineSegment StartX=110.062 StartY=-13.7374 StartZ=0 EndX=110.062 EndY=-10.1218 EndZ=0
    g235: LineSegment StartX=110.062 StartY=-10.1218 StartZ=0 EndX=105.732 EndY=-7.62179 EndZ=0
    g236: LineSegment StartX=105.732 StartY=-7.62179 StartZ=0 EndX=101.402 EndY=-10.1218 EndZ=0
    g237: LineSegment StartX=101.402 StartY=-10.1218 StartZ=0 EndX=101.402 EndY=-13.7374 EndZ=0
    g238: LineSegment StartX=114.732 StartY=9.97629 StartZ=0 EndX=114.732 EndY=14.9763 EndZ=0
    g239: LineSegment StartX=106.072 StartY=14.9763 StartZ=0 EndX=106.072 EndY=9.97629 EndZ=0
    g240: LineSegment StartX=106.072 StartY=9.97629 StartZ=0 EndX=110.402 EndY=7.47629 EndZ=0
    g241: LineSegment StartX=110.402 StartY=7.47629 StartZ=0 EndX=114.732 EndY=9.97629 EndZ=0
    g242: LineSegment StartX=119.562 StartY=1.61026 StartZ=0 EndX=119.562 EndY=6.61026 EndZ=0
    g243: LineSegment StartX=119.562 StartY=6.61026 StartZ=0 EndX=115.232 EndY=9.11026 EndZ=0
    g244: LineSegment StartX=115.232 StartY=9.11026 StartZ=0 EndX=110.902 EndY=6.61026 EndZ=0
    g245: LineSegment StartX=110.902 StartY=6.61026 StartZ=0 EndX=110.902 EndY=1.61026 EndZ=0
    g246: LineSegment StartX=110.902 StartY=1.61026 StartZ=0 EndX=115.232 EndY=-0.889736 EndZ=0
    g247: LineSegment StartX=115.232 StartY=-0.889736 StartZ=0 EndX=119.562 EndY=1.61026 EndZ=0
    g248: LineSegment StartX=114.732 StartY=-6.75576 StartZ=0 EndX=114.732 EndY=-1.75576 EndZ=0
    g249: LineSegment StartX=114.732 StartY=-1.75576 StartZ=0 EndX=110.402 EndY=0.744239 EndZ=0
    g250: LineSegment StartX=110.402 StartY=0.744239 StartZ=0 EndX=106.072 EndY=-1.75576 EndZ=0
    g251: LineSegment StartX=106.072 StartY=-1.75576 StartZ=0 EndX=106.072 EndY=-6.75576 EndZ=0
    g252: LineSegment StartX=106.072 StartY=-6.75576 StartZ=0 EndX=110.402 EndY=-9.25576 EndZ=0
    g253: LineSegment StartX=110.402 StartY=-9.25576 StartZ=0 EndX=114.732 EndY=-6.75576 EndZ=0
    g254: LineSegment StartX=119.562 StartY=-13.7374 StartZ=0 EndX=119.562 EndY=-10.1218 EndZ=0
    g255: LineSegment StartX=119.562 StartY=-10.1218 StartZ=0 EndX=115.232 EndY=-7.62179 EndZ=0
    g256: LineSegment StartX=115.232 StartY=-7.62179 StartZ=0 EndX=110.902 EndY=-10.1218 EndZ=0
    g257: LineSegment StartX=110.902 StartY=-10.1218 StartZ=0 EndX=110.902 EndY=-13.7374 EndZ=0
    g258: LineSegment StartX=124.232 StartY=9.97629 StartZ=0 EndX=124.232 EndY=14.9763 EndZ=0
    g259: LineSegment StartX=115.572 StartY=14.9763 StartZ=0 EndX=115.572 EndY=9.97629 EndZ=0
    g260: LineSegment StartX=115.572 StartY=9.97629 StartZ=0 EndX=119.902 EndY=7.47629 EndZ=0
    g261: LineSegment StartX=119.902 StartY=7.47629 StartZ=0 EndX=124.232 EndY=9.97629 EndZ=0
    g262: LineSegment StartX=129.062 StartY=1.61026 StartZ=0 EndX=129.062 EndY=6.61026 EndZ=0
    g263: LineSegment StartX=129.062 StartY=6.61026 StartZ=0 EndX=124.732 EndY=9.11026 EndZ=0
    g264: LineSegment StartX=124.732 StartY=9.11026 StartZ=0 EndX=120.402 EndY=6.61026 EndZ=0
    g265: LineSegment StartX=120.402 StartY=6.61026 StartZ=0 EndX=120.402 EndY=1.61026 EndZ=0
    g266: LineSegment StartX=120.402 StartY=1.61026 StartZ=0 EndX=124.732 EndY=-0.889736 EndZ=0
    g267: LineSegment StartX=124.732 StartY=-0.889736 StartZ=0 EndX=129.062 EndY=1.61026 EndZ=0
    g268: LineSegment StartX=124.232 StartY=-6.75576 StartZ=0 EndX=124.232 EndY=-1.75576 EndZ=0
    g269: LineSegment StartX=124.232 StartY=-1.75576 StartZ=0 EndX=119.902 EndY=0.744239 EndZ=0
    g270: LineSegment StartX=119.902 StartY=0.744239 StartZ=0 EndX=115.572 EndY=-1.75576 EndZ=0
    g271: LineSegment StartX=115.572 StartY=-1.75576 StartZ=0 EndX=115.572 EndY=-6.75576 EndZ=0
    g272: LineSegment StartX=115.572 StartY=-6.75576 StartZ=0 EndX=119.902 EndY=-9.25576 EndZ=0
    g273: LineSegment StartX=119.902 StartY=-9.25576 StartZ=0 EndX=124.232 EndY=-6.75576 EndZ=0
    g274: LineSegment StartX=129.062 StartY=-13.7374 StartZ=0 EndX=129.062 EndY=-10.1218 EndZ=0
    g275: LineSegment StartX=129.062 StartY=-10.1218 StartZ=0 EndX=124.732 EndY=-7.62179 EndZ=0
    g276: LineSegment StartX=124.732 StartY=-7.62179 StartZ=0 EndX=120.402 EndY=-10.1218 EndZ=0
    g277: LineSegment StartX=120.402 StartY=-10.1218 StartZ=0 EndX=120.402 EndY=-13.7374 EndZ=0
    g278: LineSegment StartX=133.732 StartY=9.97629 StartZ=0 EndX=133.732 EndY=14.9763 EndZ=0
    g279: LineSegment StartX=125.072 StartY=14.9763 StartZ=0 EndX=125.072 EndY=9.97629 EndZ=0
    g280: LineSegment StartX=125.072 StartY=9.97629 StartZ=0 EndX=129.402 EndY=7.47629 EndZ=0
    g281: LineSegment StartX=129.402 StartY=7.47629 StartZ=0 EndX=133.732 EndY=9.97629 EndZ=0
    g282: LineSegment StartX=138.562 StartY=1.61026 StartZ=0 EndX=138.562 EndY=6.61026 EndZ=0
    g283: LineSegment StartX=138.562 StartY=6.61026 StartZ=0 EndX=134.232 EndY=9.11026 EndZ=0
    g284: LineSegment StartX=134.232 StartY=9.11026 StartZ=0 EndX=129.902 EndY=6.61026 EndZ=0
    g285: LineSegment StartX=129.902 StartY=6.61026 StartZ=0 EndX=129.902 EndY=1.61026 EndZ=0
    g286: LineSegment StartX=129.902 StartY=1.61026 StartZ=0 EndX=134.232 EndY=-0.889736 EndZ=0
    g287: LineSegment StartX=134.232 StartY=-0.889736 StartZ=0 EndX=138.562 EndY=1.61026 EndZ=0
    g288: LineSegment StartX=133.732 StartY=-6.75576 StartZ=0 EndX=133.732 EndY=-1.75576 EndZ=0
    g289: LineSegment StartX=133.732 StartY=-1.75576 StartZ=0 EndX=129.402 EndY=0.744239 EndZ=0
    g290: LineSegment StartX=129.402 StartY=0.744239 StartZ=0 EndX=125.072 EndY=-1.75576 EndZ=0
    g291: LineSegment StartX=125.072 StartY=-1.75576 StartZ=0 EndX=125.072 EndY=-6.75576 EndZ=0
    g292: LineSegment StartX=125.072 StartY=-6.75576 StartZ=0 EndX=129.402 EndY=-9.25576 EndZ=0
    g293: LineSegment StartX=129.402 StartY=-9.25576 StartZ=0 EndX=133.732 EndY=-6.75576 EndZ=0
    g294: LineSegment StartX=138.562 StartY=-13.7374 StartZ=0 EndX=138.562 EndY=-10.1218 EndZ=0
    g295: LineSegment StartX=138.562 StartY=-10.1218 StartZ=0 EndX=134.232 EndY=-7.62179 EndZ=0
    g296: LineSegment StartX=134.232 StartY=-7.62179 StartZ=0 EndX=129.902 EndY=-10.1218 EndZ=0
    g297: LineSegment StartX=129.902 StartY=-10.1218 StartZ=0 EndX=129.902 EndY=-13.7374 EndZ=0
    g298: LineSegment StartX=143.232 StartY=9.97629 StartZ=0 EndX=143.232 EndY=14.9763 EndZ=0
    g299: LineSegment StartX=134.572 StartY=14.9763 StartZ=0 EndX=134.572 EndY=9.97629 EndZ=0
    g300: LineSegment StartX=134.572 StartY=9.97629 StartZ=0 EndX=138.902 EndY=7.47629 EndZ=0
    g301: LineSegment StartX=138.902 StartY=7.47629 StartZ=0 EndX=143.232 EndY=9.97629 EndZ=0
    g302: LineSegment StartX=144.704 StartY=8.54893 StartZ=0 EndX=143.732 EndY=9.11026 EndZ=0
    g303: LineSegment StartX=143.732 StartY=9.11026 StartZ=0 EndX=139.402 EndY=6.61026 EndZ=0
    g304: LineSegment StartX=139.402 StartY=6.61026 StartZ=0 EndX=139.402 EndY=1.61026 EndZ=0
    g305: LineSegment StartX=139.402 StartY=1.61026 StartZ=0 EndX=143.732 EndY=-0.889736 EndZ=0
    g306: LineSegment StartX=143.732 StartY=-0.889736 StartZ=0 EndX=144.704 EndY=-0.328404 EndZ=0
    g307: LineSegment StartX=143.232 StartY=-6.75576 StartZ=0 EndX=143.232 EndY=-1.75576 EndZ=0
    g308: LineSegment StartX=143.232 StartY=-1.75576 StartZ=0 EndX=138.902 EndY=0.744239 EndZ=0
    g309: LineSegment StartX=138.902 StartY=0.744239 StartZ=0 EndX=134.572 EndY=-1.75576 EndZ=0
    g310: LineSegment StartX=134.572 StartY=-1.75576 StartZ=0 EndX=134.572 EndY=-6.75576 EndZ=0
    g311: LineSegment StartX=134.572 StartY=-6.75576 StartZ=0 EndX=138.902 EndY=-9.25576 EndZ=0
    g312: LineSegment StartX=138.902 StartY=-9.25576 StartZ=0 EndX=143.232 EndY=-6.75576 EndZ=0
    g313: LineSegment StartX=143.732 StartY=-7.62179 StartZ=0 EndX=139.402 EndY=-10.1218 EndZ=0
    g314: LineSegment StartX=139.402 StartY=-10.1218 StartZ=0 EndX=139.402 EndY=-13.7374 EndZ=0
    g315: LineSegment StartX=144.704 StartY=8.54893 StartZ=0 EndX=144.704 EndY=-0.328404 EndZ=0
    g316: LineSegment StartX=144.704 StartY=-8.18312 StartZ=0 EndX=144.704 EndY=-13.7374 EndZ=0
    g317: LineSegment StartX=143.732 StartY=-7.62179 StartZ=0 EndX=144.704 EndY=-8.18312 EndZ=0
    g318: LineSegment StartX=1.57196 StartY=14.9763 StartZ=0 EndX=1.57196 EndY=14.9763 EndZ=0
    g319: LineSegment StartX=11.072 StartY=14.9763 StartZ=0 EndX=11.072 EndY=14.9763 EndZ=0
    g320: LineSegment StartX=20.572 StartY=14.9763 StartZ=0 EndX=20.572 EndY=14.9763 EndZ=0
    g321: LineSegment StartX=30.072 StartY=14.9763 StartZ=0 EndX=30.072 EndY=14.9763 EndZ=0
    g322: LineSegment StartX=39.572 StartY=14.9763 StartZ=0 EndX=39.572 EndY=14.9763 EndZ=0
    g323: LineSegment StartX=49.072 StartY=14.9763 StartZ=0 EndX=49.072 EndY=14.9763 EndZ=0
    g324: LineSegment StartX=58.572 StartY=14.9763 StartZ=0 EndX=58.572 EndY=14.9763 EndZ=0
    g325: LineSegment StartX=68.072 StartY=14.9763 StartZ=0 EndX=68.072 EndY=14.9763 EndZ=0
    g326: LineSegment StartX=77.572 StartY=14.9763 StartZ=0 EndX=77.572 EndY=14.9763 EndZ=0
    g327: LineSegment StartX=87.072 StartY=14.9763 StartZ=0 EndX=87.072 EndY=14.9763 EndZ=0
    g328: LineSegment StartX=96.572 StartY=14.9763 StartZ=0 EndX=96.572 EndY=14.9763 EndZ=0
    g329: LineSegment StartX=143.232 StartY=14.9763 StartZ=0 EndX=134.572 EndY=14.9763 EndZ=0
    g330: LineSegment StartX=133.732 StartY=14.9763 StartZ=0 EndX=125.072 EndY=14.9763 EndZ=0
    g331: LineSegment StartX=124.232 StartY=14.9763 StartZ=0 EndX=115.572 EndY=14.9763 EndZ=0
    g332: LineSegment StartX=114.732 StartY=14.9763 StartZ=0 EndX=106.072 EndY=14.9763 EndZ=0
    g333: LineSegment StartX=96.572 StartY=14.9763 StartZ=0 EndX=96.572 EndY=14.9763 EndZ=0
    g334: LineSegment StartX=87.072 StartY=14.9763 StartZ=0 EndX=95.7322 EndY=14.9763 EndZ=0
    g335: LineSegment StartX=96.572 StartY=14.9763 StartZ=0 EndX=105.232 EndY=14.9763 EndZ=0
    g336: LineSegment StartX=96.572 StartY=9.97629 StartZ=0 EndX=96.572 EndY=14.9763 EndZ=0
    g337: LineSegment StartX=77.572 StartY=14.9763 StartZ=0 EndX=86.2322 EndY=14.9763 EndZ=0
    g338: LineSegment StartX=1.57196 StartY=14.9763 StartZ=0 EndX=10.2322 EndY=14.9763 EndZ=0
    g339: LineSegment StartX=11.072 StartY=14.9763 StartZ=0 EndX=19.7322 EndY=14.9763 EndZ=0
    g340: LineSegment StartX=20.572 StartY=14.9763 StartZ=0 EndX=29.2322 EndY=14.9763 EndZ=0
    g341: LineSegment StartX=30.072 StartY=14.9763 StartZ=0 EndX=38.7322 EndY=14.9763 EndZ=0
    g342: LineSegment StartX=39.572 StartY=14.9763 StartZ=0 EndX=48.2322 EndY=14.9763 EndZ=0
    g343: LineSegment StartX=49.072 StartY=14.9763 StartZ=0 EndX=57.7322 EndY=14.9763 EndZ=0
    g344: LineSegment StartX=58.572 StartY=14.9763 StartZ=0 EndX=67.2322 EndY=14.9763 EndZ=0
    g345: LineSegment StartX=68.072 StartY=14.9763 StartZ=0 EndX=76.7322 EndY=14.9763 EndZ=0
    g346: LineSegment StartX=6.40209 StartY=-13.7374 StartZ=0 EndX=15.0623 EndY=-13.7374 EndZ=0
    g347: LineSegment StartX=1.57196 StartY=9.97629 StartZ=0 EndX=1.57196 EndY=9.97629 EndZ=0
    g348: LineSegment StartX=5.56209 StartY=1.81557 StartZ=0 EndX=1.57196 EndY=-0.482386 EndZ=0
    g349: LineSegment StartX=19.7322 StartY=-1.75576 StartZ=0 EndX=19.7255 EndY=-1.75188 EndZ=0
    g350: LineSegment StartX=5.56209 StartY=6.42569 StartZ=0 EndX=1.57196 EndY=8.72948 EndZ=0
    g351: LineSegment StartX=5.56209 StartY=6.42569 StartZ=0 EndX=5.56209 EndY=1.81557 EndZ=0
    g352: LineSegment StartX=1.57196 StartY=-0.482386 StartZ=0 EndX=1.57196 EndY=8.72948 EndZ=0
    g353: LineSegment StartX=1.57196 StartY=9.97629 StartZ=0 EndX=5.90209 EndY=7.47629 EndZ=0
    g354: LineSegment StartX=19.7255 StartY=-1.75188 StartZ=0 EndX=15.4021 EndY=0.744239 EndZ=0
    g355: LineSegment StartX=1.57196 StartY=-7.81244 StartZ=0 EndX=1.57196 EndY=-13.7374 EndZ=0
    g356: LineSegment StartX=5.56209 StartY=-13.7374 StartZ=0 EndX=1.57196 EndY=-13.7374 EndZ=0
    g357: LineSegment StartX=5.56209 StartY=-10.1218 StartZ=0 EndX=5.56209 EndY=-13.7374 EndZ=0
    g358: LineSegment StartX=5.56209 StartY=-10.1218 StartZ=0 EndX=1.57196 EndY=-7.81244 EndZ=0
    g359: LineSegment StartX=24.5623 StartY=-13.7374 StartZ=0 EndX=15.9021 EndY=-13.7374 EndZ=0
    g360: LineSegment StartX=34.0623 StartY=-13.7374 StartZ=0 EndX=25.4021 EndY=-13.7374 EndZ=0
    g361: LineSegment StartX=43.5623 StartY=-13.7374 StartZ=0 EndX=34.9021 EndY=-13.7374 EndZ=0
    g362: LineSegment StartX=53.0623 StartY=-13.7374 StartZ=0 EndX=44.4021 EndY=-13.7374 EndZ=0
    g363: LineSegment StartX=62.5623 StartY=-13.7374 StartZ=0 EndX=53.9021 EndY=-13.7374 EndZ=0
    g364: LineSegment StartX=72.0623 StartY=-13.7374 StartZ=0 EndX=63.4021 EndY=-13.7374 EndZ=0
    g365: LineSegment StartX=81.5623 StartY=-13.7374 StartZ=0 EndX=72.9021 EndY=-13.7374 EndZ=0
    g366: LineSegment StartX=91.0623 StartY=-13.7374 StartZ=0 EndX=82.4021 EndY=-13.7374 EndZ=0
    g367: LineSegment StartX=100.562 StartY=-13.7374 StartZ=0 EndX=91.9021 EndY=-13.7374 EndZ=0
    g368: LineSegment StartX=110.062 StartY=-13.7374 StartZ=0 EndX=101.402 EndY=-13.7374 EndZ=0
    g369: LineSegment StartX=119.562 StartY=-13.7374 StartZ=0 EndX=110.902 EndY=-13.7374 EndZ=0
    g370: LineSegment StartX=129.062 StartY=-13.7374 StartZ=0 EndX=120.402 EndY=-13.7374 EndZ=0
    g371: LineSegment StartX=138.562 StartY=-13.7374 StartZ=0 EndX=129.902 EndY=-13.7374 EndZ=0
    g372: LineSegment StartX=144.704 StartY=-13.7374 StartZ=0 EndX=139.402 EndY=-13.7374 EndZ=0
    g373: LineSegment StartX=1.57196 StartY=9.97629 StartZ=0 EndX=1.57196 EndY=14.9763 EndZ=0
  constraints (550):
    c: Vertical(g0)
    c: Coincident(g0,g1)
    c: Vertical(g3)
    c: Coincident(g4,g0)
    c: Vertical(g5)
    c: Coincident(g5,g6)
    c: Coincident(g6,g7)
    c: Coincident(g7,g8)
    c: Vertical(g8)
    c: Coincident(g8,g9)
    c: Coincident(g9,g10)
    c: Coincident(g10,g5)
    c: Vertical(g11)
    c: Coincident(g11,g12)
    c: Coincident(g12,g13)
    c: Coincident(g13,g14)
    c: Vertical(g14)
    c: Coincident(g14,g15)
    c: Coincident(g15,g16)
    c: Coincident(g16,g11)
    c: Vertical(g17)
    c: Coincident(g17,g18)
    c: Coincident(g18,g19)
    c: Coincident(g19,g20)
    c: Vertical(g20)
    c: Vertical(g21)
    c: Coincident(g21,g22)
    c: Coincident(g23,g24)
    c: Vertical(g24)
    c: Coincident(g24,g25)
    c: Coincident(g25,g26)
    c: Coincident(g26,g21)
    c: Vertical(g27)
    c: Coincident(g27,g28)
    c: Coincident(g28,g29)
    c: Coincident(g29,g30)
    c: Vertical(g30)
    c: Coincident(g30,g31)
    c: Coincident(g31,g32)
    c: Coincident(g32,g27)
    c: Vertical(g33)
    c: Coincident(g34,g35)
    c: Vertical(g35)
    c: Coincident(g35,g36)
    c: Coincident(g36,g37)
    c: Coincident(g37,g33)
    c: Vertical(g38)
    c: Coincident(g38,g39)
    c: Coincident(g39,g40)
    c: Coincident(g40,g41)
    c: Vertical(g41)
    c: Vertical(g42)
    c: Coincident(g42,g43)
    c: Coincident(g44,g45)
    c: Vertical(g45)
    c: Coincident(g45,g46)
    c: Coincident(g46,g47)
    c: Coincident(g47,g42)
    c: Vertical(g48)
    c: Coincident(g48,g49)
    c: Coincident(g49,g50)
    c: Coincident(g50,g51)
    c: Vertical(g51)
    c: Coincident(g51,g52)
    c: Coincident(g52,g53)
    c: Coincident(g53,g48)
    c: Vertical(g54)
    c: Coincident(g54,g55)
    c: Coincident(g55,g56)
    c: Coincident(g56,g57)
    c: Vertical(g57)
    c: Coincident(g57,g58)
    c: Coincident(g58,g59)
    c: Coincident(g59,g54)
    c: Vertical(g60)
    c: Coincident(g60,g61)
    c: Coincident(g61,g62)
    c: Coincident(g62,g63)
    c: Vertical(g63)
    c: Vertical(g64)
    c: Coincident(g64,g65)
    c: Coincident(g66,g67)
    c: Vertical(g67)
    c: Coincident(g67,g68)
    c: Coincident(g68,g69)
    c: Coincident(g69,g64)
    c: Vertical(g70)
    c: Coincident(g70,g71)
    c: Coincident(g71,g72)
    c: Coincident(g72,g73)
    c: Vertical(g73)
    c: Coincident(g73,g74)
    c: Coincident(g74,g75)
    c: Coincident(g75,g70)
    c: Vertical(g76)
    c: Coincident(g76,g77)
    c: Coincident(g77,g78)
    c: Coincident(g78,g79)
    c: Vertical(g79)
    c: Coincident(g79,g80)
    c: Coincident(g80,g81)
    c: Coincident(g81,g76)
    c: Vertical(g82)
    c: Coincident(g82,g83)
    c: Coincident(g83,g84)
    c: Coincident(g84,g85)
    c: Vertical(g85)
    c: Vertical(g86)
    c: Coincident(g86,g87)
    c: Coincident(g88,g89)
    c: Vertical(g89)
    c: Coincident(g89,g90)
    c: Coincident(g90,g91)
    c: Coincident(g91,g86)
    c: Vertical(g92)
    c: Coincident(g92,g93)
    c: Coincident(g93,g94)
    c: Coincident(g94,g95)
    c: Vertical(g95)
    c: Coincident(g95,g96)
    c: Coincident(g96,g97)
    c: Coincident(g97,g92)
    c: Vertical(g98)
    c: Coincident(g98,g99)
    c: Coincident(g99,g100)
    c: Coincident(g100,g101)
    c: Vertical(g101)
    c: Coincident(g101,g102)
    c: Coincident(g102,g103)
    c: Coincident(g103,g98)
    c: Vertical(g104)
    c: Coincident(g104,g105)
    c: Coincident(g105,g106)
    c: Coincident(g106,g107)
    c: Vertical(g107)
    c: Vertical(g108)
    c: Coincident(g108,g109)
    c: Coincident(g110,g111)
    c: Vertical(g111)
    c: Coincident(g111,g112)
    c: Coincident(g112,g113)
    c: Coincident(g113,g108)
    c: Vertical(g114)
    c: Coincident(g114,g115)
    c: Coincident(g115,g116)
    c: Coincident(g116,g117)
    c: Vertical(g117)
    c: Coincident(g117,g118)
    c: Coincident(g118,g119)
    c: Coincident(g119,g114)
    c: Vertical(g120)
    c: Coincident(g120,g121)
    c: Coincident(g121,g122)
    c: Coincident(g122,g123)
    c: Vertical(g123)
    c: Coincident(g123,g124)
    c: Coincident(g124,g125)
    c: Coincident(g125,g120)
    c: Vertical(g126)
    c: Coincident(g126,g127)
    c: Coincident(g127,g128)
    c: Coincident(g128,g129)
    c: Vertical(g129)
    c: Vertical(g130)
    c: Coincident(g130,g131)
    c: Coincident(g132,g133)
    c: Vertical(g133)
    c: Coincident(g133,g134)
    c: Coincident(g134,g135)
    c: Coincident(g135,g130)
    c: Vertical(g136)
    c: Coincident(g136,g137)
    c: Coincident(g137,g138)
    c: Coincident(g138,g139)
    c: Vertical(g139)
    c: Coincident(g139,g140)
    c: Coincident(g140,g141)
    c: Coincident(g141,g136)
    c: Vertical(g142)
    c: Coincident(g142,g143)
    c: Coincident(g143,g144)
    c: Coincident(g144,g145)
    c: Vertical(g145)
    c: Coincident(g145,g146)
    c: Coincident(g146,g147)
    c: Coincident(g147,g142)
    c: Vertical(g148)
    c: Coincident(g148,g149)
    c: Coincident(g149,g150)
    c: Coincident(g150,g151)
    c: Vertical(g151)
    c: Vertical(g152)
    c: Coincident(g152,g153)
    c: Coincident(g154,g155)
    c: Vertical(g155)
    c: Coincident(g155,g156)
    c: Coincident(g156,g157)
    c: Coincident(g157,g152)
    c: Vertical(g158)
    c: Coincident(g158,g159)
    c: Coincident(g159,g160)
    c: Coincident(g160,g161)
    c: Vertical(g161)
    c: Coincident(g161,g162)
    c: Coincident(g162,g163)
    c: Coincident(g163,g158)
    c: Vertical(g164)
    c: Coincident(g164,g165)
    c: Coincident(g165,g166)
    c: Coincident(g166,g167)
    c: Vertical(g167)
    c: Coincident(g167,g168)
    c: Coincident(g168,g169)
    c: Coincident(g169,g164)
    c: Vertical(g170)
    c: Coincident(g170,g171)
    c: Coincident(g171,g172)
    c: Coincident(g172,g173)
    c: Vertical(g173)
    c: Vertical(g174)
    c: Coincident(g174,g175)
    c: Coincident(g176,g177)
    c: Vertical(g177)
    c: Coincident(g177,g178)
    c: Coincident(g178,g179)
    c: Coincident(g179,g174)
    c: Vertical(g180)
    c: Coincident(g180,g181)
    c: Coincident(g181,g182)
    c: Coincident(g182,g183)
    c: Vertical(g183)
    c: Coincident(g183,g184)
    c: Coincident(g184,g185)
    c: Coincident(g185,g180)
    c: Vertical(g186)
    c: Coincident(g186,g187)
    c: Coincident(g187,g188)
    c: Coincident(g188,g189)
    c: Vertical(g189)
    c: Coincident(g189,g190)
    c: Coincident(g190,g191)
    c: Coincident(g191,g186)
    c: Vertical(g192)
    c: Coincident(g192,g193)
    c: Coincident(g193,g194)
    c: Coincident(g194,g195)
    c: Vertical(g195)
    c: Vertical(g196)
    c: Coincident(g196,g197)
    c: Coincident(g198,g199)
    c: Vertical(g199)
    c: Coincident(g199,g200)
    c: Coincident(g200,g201)
    c: Coincident(g201,g196)
    c: Vertical(g202)
    c: Coincident(g202,g203)
    c: Coincident(g203,g204)
    c: Coincident(g204,g205)
    c: Vertical(g205)
    c: Coincident(g205,g206)
    c: Coincident(g206,g207)
    c: Coincident(g207,g202)
    c: Vertical(g208)
    c: Coincident(g208,g209)
    c: Coincident(g209,g210)
    c: Coincident(g210,g211)
    c: Vertical(g211)
    c: Coincident(g211,g212)
    c: Coincident(g212,g213)
    c: Coincident(g213,g208)
    c: Vertical(g214)
    c: Coincident(g214,g215)
    c: Coincident(g215,g216)
    c: Coincident(g216,g217)
    c: Vertical(g217)
    c: Vertical(g218)
    c: Coincident(g220,g221)
    c: Coincident(g221,g218)
    c: Vertical(g222)
    c: Coincident(g222,g223)
    c: Coincident(g223,g224)
    c: Coincident(g224,g225)
    c: Vertical(g225)
    c: Coincident(g225,g226)
    c: Coincident(g226,g227)
    c: Coincident(g227,g222)
    c: Vertical(g228)
    c: Coincident(g228,g229)
    c: Coincident(g229,g230)
    c: Coincident(g230,g231)
    c: Vertical(g231)
    c: Coincident(g231,g232)
    c: Coincident(g232,g233)
    c: Coincident(g233,g228)
    c: Vertical(g234)
    c: Coincident(g234,g235)
    c: Coincident(g235,g236)
    c: Coincident(g236,g237)
    c: Vertical(g237)
    c: Vertical(g238)
    c: Vertical(g239)
    c: Coincident(g239,g240)
    c: Coincident(g240,g241)
    c: Coincident(g241,g238)
    c: Vertical(g242)
    c: Coincident(g242,g243)
    c: Coincident(g243,g244)
    c: Coincident(g244,g245)
    c: Vertical(g245)
    c: Coincident(g245,g246)
    c: Coincident(g246,g247)
    c: Coincident(g247,g242)
    c: Vertical(g248)
    c: Coincident(g248,g249)
    c: Coincident(g249,g250)
    c: Coincident(g250,g251)
    c: Vertical(g251)
    c: Coincident(g251,g252)
    c: Coincident(g252,g253)
    c: Coincident(g253,g248)
    c: Vertical(g254)
    c: Coincident(g254,g255)
    c: Coincident(g255,g256)
    c: Coincident(g256,g257)
    c: Vertical(g257)
    c: Vertical(g258)
    c: Vertical(g259)
    c: Coincident(g259,g260)
    c: Coincident(g260,g261)
    c: Coincident(g261,g258)
    c: Vertical(g262)
    c: Coincident(g262,g263)
    c: Coincident(g263,g264)
    c: Coincident(g264,g265)
    c: Vertical(g265)
    c: Coincident(g265,g266)
    c: Coincident(g266,g267)
    c: Coincident(g267,g262)
    c: Vertical(g268)
    c: Coincident(g268,g269)
    c: Coincident(g269,g270)
    c: Coincident(g270,g271)
    c: Vertical(g271)
    c: Coincident(g271,g272)
    c: Coincident(g272,g273)
    c: Coincident(g273,g268)
    c: Vertical(g274)
    c: Coincident(g274,g275)
    c: Coincident(g275,g276)
    c: Coincident(g276,g277)
    c: Vertical(g277)
    c: Vertical(g278)
    c: Vertical(g279)
    c: Coincident(g279,g280)
    c: Coincident(g280,g281)
    c: Coincident(g281,g278)
    c: Vertical(g282)
    c: Coincident(g282,g283)
    c: Coincident(g283,g284)
    c: Coincident(g284,g285)
    c: Vertical(g285)
    c: Coincident(g285,g286)
    c: Coincident(g286,g287)
    c: Coincident(g287,g282)
    c: Vertical(g288)
    c: Coincident(g288,g289)
    c: Coincident(g289,g290)
    c: Coincident(g290,g291)
    c: Vertical(g291)
    c: Coincident(g291,g292)
    c: Coincident(g292,g293)
    c: Coincident(g293,g288)
    c: Vertical(g294)
    c: Coincident(g294,g295)
    c: Coincident(g295,g296)
    c: Coincident(g296,g297)
    c: Vertical(g297)
    c: Vertical(g298)
    c: Vertical(g299)
    c: Coincident(g299,g300)
    c: Coincident(g300,g301)
    c: Coincident(g301,g298)
    c: Coincident(g302,g303)
    c: Coincident(g303,g304)
    c: Vertical(g304)
    c: Coincident(g304,g305)
    c: Coincident(g305,g306)
    c: Vertical(g307)
    c: Coincident(g307,g308)
    c: Coincident(g308,g309)
    c: Coincident(g309,g310)
    c: Vertical(g310)
    c: Coincident(g310,g311)
    c: Coincident(g311,g312)
    c: Coincident(g312,g307)
    c: Coincident(g313,g314)
    c: Vertical(g314)
    c: Vertical(g315)
    c: Coincident(g315,g306)
    c: Coincident(g315,g302)
    c: Coincident(g317,g313)
    c: Coincident(g317,g316)
    c: Coincident(g318,g2)
    c: Coincident(g319,g23)
    c: Coincident(g320,g44)
    c: Coincident(g321,g66)
    c: Horizontal(g321)
    c: Coincident(g322,g88)
    c: Coincident(g323,g110)
    c: Coincident(g324,g132)
    c: Coincident(g325,g154)
    c: Coincident(g326,g176)
    c: Horizontal(g326)
    c: Coincident(g327,g198)
    c: Horizontal(g327)
    c: Coincident(g328,g219)
    c: Horizontal(g328)
    c: Coincident(g329,g298)
    c: Coincident(g329,g299)
    c: Horizontal(g329)
    c: Coincident(g330,g278)
    c: Coincident(g330,g279)
    c: Horizontal(g330)
    c: Coincident(g331,g258)
    c: Coincident(g331,g259)
    c: Horizontal(g331)
    c: Coincident(g332,g238)
    c: Coincident(g332,g239)
    c: Horizontal(g332)
    c: Coincident(g219,g328)
    c: PointOnObject(g197,g327)
    c: Coincident(g327,g198)
    c: Coincident(g334,g198)
    c: Coincident(g334,g197)
    c: Horizontal(g334)
    c: PointOnObject(g333,g219)
    c: Coincident(g335,g333)
    c: Coincident(g335,g218)
    c: Horizontal(g335)
    c: Coincident(g336,g220)
    c: Coincident(g336,g333)
    c: Vertical(g336)
    c: PointOnObject(g175,g326)
    c: Coincident(g326,g176)
    c: Coincident(g337,g176)
    c: Coincident(g337,g175)
    c: Horizontal(g337)
    c: PointOnObject(g153,g325)
    c: Coincident(g325,g154)
    c: PointOnObject(g131,g324)
    c: Coincident(g132,g324)
    c: PointOnObject(g109,g323)
    c: Coincident(g323,g110)
    c: PointOnObject(g87,g322)
    c: Coincident(g88,g322)
    c: PointOnObject(g65,g321)
    c: Coincident(g321,g66)
    c: PointOnObject(g43,g320)
    c: Coincident(g320,g44)
    c: PointOnObject(g22,g319)
    c: Coincident(g319,g23)
    c: PointOnObject(g1,g318)
    c: Coincident(g318,g2)
    c: Coincident(g338,g2)
    c: Coincident(g338,g1)
    c: Horizontal(g338)
    c: Coincident(g339,g23)
    c: Coincident(g339,g22)
    c: Horizontal(g339)
    c: Coincident(g340,g44)
    c: Coincident(g340,g43)
    c: Horizontal(g340)
    c: Coincident(g341,g66)
    c: Coincident(g341,g65)
    c: Horizontal(g341)
    c: Coincident(g342,g88)
    c: Coincident(g342,g87)
    c: Horizontal(g342)
    c: Coincident(g343,g110)
    c: Coincident(g343,g109)
    c: Horizontal(g343)
    c: Coincident(g344,g132)
    c: Coincident(g344,g131)
    c: Horizontal(g344)
    c: Coincident(g345,g154)
    c: Coincident(g345,g153)
    c: Horizontal(g345)
    c: Coincident(g346,g20)
    c: Coincident(g346,g17)
    c: Coincident(g349,g33)
    c: Coincident(g350,g351)
    c: Coincident(g351,g348)
    c: Coincident(g352,g348)
    c: Coincident(g352,g350)
    c: Vertical(g352)
    c: PointOnObject(g3,g347)
    c: Coincident(g353,g3)
    c: Coincident(g353,g4)
    c: Coincident(g354,g349)
    c: Coincident(g354,g34)
    c: Angle(g18,g17) = 2.0944
    c: Coincident(g358,g357)
    c: Coincident(g355,g358)
    c: Coincident(g356,g355)
    c: Coincident(g357,g356)
    c: Coincident(g359,g38)
    c: Coincident(g359,g41)
    c: Horizontal(g359)
    c: Coincident(g360,g60)
    c: Coincident(g360,g63)
    c: Horizontal(g360)
    c: Coincident(g361,g82)
    c: Coincident(g361,g85)
    c: Horizontal(g361)
    c: Coincident(g362,g104)
    c: Coincident(g362,g107)
    c: Horizontal(g362)
    c: Coincident(g363,g126)
    c: Coincident(g363,g129)
    c: Horizontal(g363)
    c: Coincident(g364,g148)
    c: Coincident(g364,g151)
    c: Horizontal(g364)
    c: Coincident(g365,g170)
    c: Coincident(g365,g173)
    c: Horizontal(g365)
    c: Coincident(g366,g192)
    c: Coincident(g366,g195)
    c: Horizontal(g366)
    c: Coincident(g367,g214)
    c: Coincident(g367,g217)
    c: Horizontal(g367)
    c: Coincident(g368,g234)
    c: Coincident(g368,g237)
    c: Horizontal(g368)
    c: Coincident(g369,g254)
    c: Coincident(g369,g257)
    c: Horizontal(g369)
    c: Coincident(g370,g274)
    c: Coincident(g370,g277)
    c: Horizontal(g370)
    c: Coincident(g371,g294)
    c: Coincident(g371,g297)
    c: Horizontal(g371)
    c: Coincident(g372,g316)
    c: Coincident(g372,g314)
    c: Horizontal(g372)
    c: Coincident(g373,g3)
    c: Coincident(g373,g2)
    c: Vertical(g373)
FEATURE [Part::Extrusion] Extrude003
  Base = -> Sketch013
  Dir = (0,-1,2e-16)
  DirMode = 2
  FaceMakerClass = Part::FaceMakerBullseye
  FaceMakerMode = 3
  LengthFwd = 10
  LengthRev = -130
  Placement = pos=(0,126,0) rot=(0,0,1;0rad)
  Solid = true
  Symmetric = false
FEATURE [Image::ImagePlane] IMG_3574
  Placement = pos=(76,-54,-7) rot=(1,0,0;1.5708rad)
  XSize = 172.416
  YSize = 129.311
FEATURE [Sketcher::SketchObject] Sketch014
  ArcFitTolerance = 1e-06
  AttachmentSupport = -> [YZ_Plane003]
  FullyConstrained = false
  MakeInternals = false
  MapMode = 5
  Placement = pos=(0,0,0) rot=(0.57735,0.57735,0.57735;2.0944rad)
  expr: Constraints[42] = <<Medidas001>>.AnchoDisco + <<Medidas001>>.HolguraMediciones
  expr: Constraints[43] = <<Medidas001>>.GrosorSoporteHDD
  expr: Constraints[44] = <<Medidas001>>.GrosorSoporteHDD
  sketch-geometry (23):
    g0: LineSegment StartX=-48.0376 StartY=-29.8455 StartZ=0 EndX=-48.0376 EndY=-63.8455 EndZ=0
    g1: LineSegment StartX=37.0376 StartY=-18.8455 StartZ=0 EndX=-37.0376 EndY=-18.8455 EndZ=0
    g2: ArcOfCircle CenterX=-37.0376 CenterY=-29.8455 CenterZ=0 NormalX=0 NormalY=0 NormalZ=1 AngleXU=0 Radius=11 StartAngle=1.5708 EndAngle=3.14159
    g3: ArcOfCircle CenterX=37.0376 CenterY=-29.8455 CenterZ=0 NormalX=0 NormalY=0 NormalZ=1 AngleXU=0 Radius=11 StartAngle=6.02126 EndAngle=7.85398
    g4: GeomPoint [constr] X=-48.0376 Y=-18.8455 Z=0
    g5: GeomPoint [constr] X=47.85 Y=-88.4081 Z=0
    g6: LineSegment [constr] StartX=-37.0376 StartY=-18.8455 StartZ=0 EndX=-37.0376 EndY=-16.8455 EndZ=0
    g7: LineSegment StartX=-48.0376 StartY=-63.8455 StartZ=0 EndX=-52.0376 EndY=-63.8455 EndZ=0
    g8: LineSegment StartX=47.6624 StartY=-63.8453 StartZ=0 EndX=51.8467 EndY=-63.8453 EndZ=0
    g9: LineSegment StartX=-52.0376 StartY=-63.8455 StartZ=0 EndX=-52.0376 EndY=-16.8455 EndZ=0
    g10: LineSegment StartX=51.8467 StartY=-63.8453 StartZ=0 EndX=51.8467 EndY=-16.8453 EndZ=0
    g11: LineSegment StartX=47.6624 StartY=-63.8453 StartZ=0 EndX=47.6624 EndY=-32.6939 EndZ=0
    g12: LineSegment [constr] StartX=-51.85 StartY=-19.6939 StartZ=0 EndX=51.8467 EndY=-19.6937 EndZ=0
    g13: LineSegment StartX=-54.9444 StartY=18.1545 StartZ=0 EndX=54.8556 EndY=18.1547 EndZ=0
    g14: LineSegment [constr] StartX=-52.0376 StartY=-19.698 StartZ=0 EndX=51.8467 EndY=-16.9256 EndZ=0
    g15: LineSegment StartX=-54.9444 StartY=18.1545 StartZ=0 EndX=-54.9444 EndY=-16.8455 EndZ=0
    g16: LineSegment StartX=54.8556 StartY=18.1547 StartZ=0 EndX=54.8556 EndY=-16.8453 EndZ=0
    g17: LineSegment StartX=-50.9444 StartY=14.1545 StartZ=0 EndX=-50.9444 EndY=-12.8455 EndZ=0
    g18: LineSegment StartX=-50.9444 StartY=-12.8455 StartZ=0 EndX=50.8556 EndY=-12.8455 EndZ=0
    g19: LineSegment StartX=50.8556 StartY=-12.8455 StartZ=0 EndX=50.8556 EndY=14.1545 EndZ=0
    g20: LineSegment StartX=50.8556 StartY=14.1545 StartZ=0 EndX=-50.9444 EndY=14.1545 EndZ=0
    g21: LineSegment StartX=51.8467 StartY=-16.8453 StartZ=0 EndX=54.8556 EndY=-16.8453 EndZ=0
    g22: LineSegment StartX=-54.9444 StartY=-16.8455 StartZ=0 EndX=-52.0376 EndY=-16.8455 EndZ=0
  constraints (55):
    c: Tangent(g0,g2) = -1.5708
    c: Tangent(g1,g3) = -1.5708
    c: Tangent(g1,g2) = -1.5708
    c: Vertical(g0)
    c: PointOnObject(g4,g0)
    c: PointOnObject(g4,g1)
    c: Radius(g2) = 11
    c: Equal(g2,g3)
    c: Vertical(g6)
    c: Coincident(g6,g1)
    c: Distance(g6) = 2
    c: Symmetric(g1,g1,g-2)
    c: DistanceY(g0,g1) = 45
    c: Distance(g7) = 4
    c: Horizontal(g7)
    c: Coincident(g7,g0)
    c: Vertical(g9)
    c: Coincident(g9,g7)
    c: Horizontal(g8)
    c: Vertical(g10)
    c: Coincident(g10,g8)
    c: Coincident(g11,g8)
    c: Coincident(g11,g3)
    c: Vertical(g11)
    c: Coincident(g13,g15)
    c: Vertical(g16)
    c: PointOnObject(g16,g14)
    c: Coincident(g13,g16)
    c: Distance(g13) = 109.8
    c: Distance(g15) = 35
    c: Equal(g15,g16)
    c: Equal(g9,g10)
    c: Distance(g9) = 47
    c: DistanceX(g0,g8) = 95.7
    c: Coincident(g17,g18)
    c: Coincident(g18,g19)
    c: Coincident(g19,g20)
    c: Coincident(g20,g17)
    c: Vertical(g17)
    c: Vertical(g19)
    c: Horizontal(g18)
    c: Horizontal(g20)
    c: Distance(g18) = 101.8
    c: DistanceX(g13,g17) = 4
    c: DistanceX(g19,g13) = 4
    c: PointOnObject(g14,g10)
    c: Coincident(g21,g10)
    c: Coincident(g21,g16)
    c: Horizontal(g21)
    c: PointOnObject(g14,g9)
    c: Coincident(g22,g15)
    c: Coincident(g22,g9)
    c: Horizontal(g22)
    c: Distance(g17) = 27
    c: DistanceY(g15,g17) = 4
FEATURE [PartDesign::Pad] Pad004
  Direction = (1,0,0)
  Length = 146
  Length2 = 10
  Placement = pos=(0,0,0) rot=(1,1,1;2.0944rad)
  Profile = -> Sketch014
  ReferenceAxis = -> Sketch014 [N_Axis]
  Suppressed = false
  Type = 0
FEATURE [PartDesign::Fillet] Fillet001
  Base = -> Pad004 [Edge29,Edge26,Edge23,Edge32,Edge17,Edge38]
  BaseFeature = -> Pad004
  Placement = pos=(0,0,0) rot=(1,1,1;2.0944rad)
  Radius = 2
  SupportTransform = false
  Suppressed = false
  UseAllEdges = false
FEATURE [Sketcher::SketchObject] Sketch018  label="sketchh001"
  ArcFitTolerance = 1e-06
  ExternalGeometry = -> [Sketch014]
  FullyConstrained = true
  MakeInternals = false
  MapMode = 5
  Placement = pos=(146,0,0) rot=(0.57735,0.57735,0.57735;2.0944rad)
  sketch-geometry (10):
    g0: LineSegment StartX=-54.9444 StartY=16.1545 StartZ=0 EndX=-54.9444 EndY=-14.8453 EndZ=0
    g1: LineSegment StartX=-52.9444 StartY=-16.8453 StartZ=0 EndX=52.8556 EndY=-16.8453 EndZ=0
    g2: LineSegment StartX=54.8556 StartY=-14.8453 StartZ=0 EndX=54.8556 EndY=16.1545 EndZ=0
    g3: LineSegment StartX=52.8556 StartY=18.1545 StartZ=0 EndX=-52.9444 EndY=18.1545 EndZ=0
    g4: ArcOfCircle CenterX=-52.9444 CenterY=16.1545 CenterZ=0 NormalX=0 NormalY=0 NormalZ=1 AngleXU=0 Radius=2 StartAngle=1.5708 EndAngle=3.14159
    g5: ArcOfCircle CenterX=-52.9444 CenterY=-14.8453 CenterZ=0 NormalX=0 NormalY=0 NormalZ=1 AngleXU=0 Radius=2 StartAngle=3.14159 EndAngle=4.71239
    g6: ArcOfCircle CenterX=52.8556 CenterY=-14.8453 CenterZ=0 NormalX=0 NormalY=0 NormalZ=1 AngleXU=0 Radius=2 StartAngle=4.71239 EndAngle=6.28319
    g7: ArcOfCircle CenterX=52.8556 CenterY=16.1545 CenterZ=0 NormalX=0 NormalY=0 NormalZ=1 AngleXU=0 Radius=2 StartAngle=0 EndAngle=1.5708
    g8: GeomPoint [constr] X=-54.9444 Y=18.1545 Z=0
    g9: GeomPoint [constr] X=54.8556 Y=-16.8453 Z=0
  constraints (22):
    c: Tangent(g0,g4) = -1.5708
    c: Tangent(g0,g5) = -1.5708
    c: Tangent(g1,g5) = -1.5708
    c: Tangent(g1,g6) = -1.5708
    c: Tangent(g2,g6) = -1.5708
    c: Tangent(g2,g7) = -1.5708
    c: Tangent(g3,g7) = -1.5708
    c: Tangent(g3,g4) = -1.5708
    c: Vertical(g0)
    c: Vertical(g2)
    c: Horizontal(g1)
    c: Horizontal(g3)
    c: Equal(g4,g5)
    c: Equal(g5,g6)
    c: Equal(g6,g7)
    c: PointOnObject(g8,g0)
    c: PointOnObject(g8,g3)
    c: PointOnObject(g9,g1)
    c: PointOnObject(g9,g2)
    c: Radius(g5) = 2
    c: Coincident(g8,g-4)
    c: Coincident(g9,g-6)
FEATURE [PartDesign::Pad] Pad005
  BaseFeature = -> Fillet001
  Direction = (1,-1e-16,1e-16)
  Length = 1
  Length2 = 10
  Placement = pos=(0,0,0) rot=(1,1,1;2.0944rad)
  Profile = -> Sketch018
  ReferenceAxis = -> Sketch018 [N_Axis]
  Reversed = true
  Suppressed = false
  Type = 0
FEATURE [PartDesign::Body] Body003
  AllowCompound = false
  Group = -> [Sketch014,Pad004,Fillet001,Sketch018,Pad005]
  Origin = -> Origin003
  Tip = -> Pad005
FEATURE [Spreadsheet::Sheet] Spreadsheet001  label="Medidas001"
  cells = A1='AnchoTower; B1(AnchoTower)==95.3 mm; A2='AnchoDisco; B2(AnchoDisco)==101.4 mm; A3='GrosorSoporteTower; B3(GrosorSoporteTower)==4 mm; A4='GrosorSoporteHDD; B4(GrosorSoporteHDD)==4 mm; A5='RadioAnguloTower; B5(RadioAnguloTower)==11 mm; A6='AltoSporteTower; B6(AltoSporteTower)==40 mm; A7='AltoSporteDisco; B7(AltoSporteDisco)==26 mm; A8='AltoEspacioIntermedio; B8(AltoEspacioIntermedio)==10 mm; A9='HolguraMediciones; B9(HolguraMediciones)==0.4 mm
FEATURE [Sketcher::SketchObject] Sketch004
  ArcFitTolerance = 1e-06
  FullyConstrained = true
  MakeInternals = false
  MapMode = 5
  sketch-geometry (17):
    g0: LineSegment StartX=-1e-16 StartY=-5 StartZ=0 EndX=4.33013 EndY=-2.5 EndZ=0
    g1: LineSegment StartX=4.33013 StartY=-2.5 StartZ=0 EndX=4.33013 EndY=2.5 EndZ=0
    g2: LineSegment StartX=4.33013 StartY=2.5 StartZ=0 EndX=-8e-16 EndY=5 EndZ=0
    g3: LineSegment StartX=-8e-16 StartY=5 StartZ=0 EndX=-4.33013 EndY=2.5 EndZ=0
    g4: LineSegment StartX=-4.33013 StartY=2.5 StartZ=0 EndX=-4.33013 EndY=-2.5 EndZ=0
    g5: LineSegment StartX=-4.33013 StartY=-2.5 StartZ=0 EndX=-1e-16 EndY=-5 EndZ=0
    g6: Circle [constr] CenterX=0 CenterY=0 CenterZ=0 NormalX=0 NormalY=0 NormalZ=1 AngleXU=0 Radius=5
    g7: LineSegment StartX=9.16025 StartY=-10.866 StartZ=0 EndX=9.16025 EndY=-5.86603 EndZ=0
    g8: LineSegment StartX=9.16025 StartY=-5.86603 StartZ=0 EndX=4.83013 EndY=-3.36603 EndZ=0
    g9: LineSegment StartX=4.83013 StartY=-3.36603 StartZ=0 EndX=0.5 EndY=-5.86603 EndZ=0
    g10: LineSegment StartX=0.5 StartY=-5.86603 StartZ=0 EndX=0.5 EndY=-10.866 EndZ=0
    g11: LineSegment StartX=0.5 StartY=-10.866 StartZ=0 EndX=4.83013 EndY=-13.366 EndZ=0
    g12: LineSegment StartX=4.83013 StartY=-13.366 StartZ=0 EndX=9.16025 EndY=-10.866 EndZ=0
    g13: Circle [constr] CenterX=4.83013 CenterY=-8.36603 CenterZ=0 NormalX=0 NormalY=0 NormalZ=1 AngleXU=0 Radius=5
    g14: LineSegment [constr] StartX=4.33013 StartY=-2.5 StartZ=0 EndX=4.83013 EndY=-3.36603 EndZ=0
    g15: LineSegment [constr] StartX=4.83013 StartY=-3.36603 StartZ=0 EndX=5.33013 EndY=-2.5 EndZ=0
    g16: LineSegment [constr] StartX=5.33013 StartY=-2.5 StartZ=0 EndX=4.33013 EndY=-2.5 EndZ=0
  constraints (40):
    c: Coincident(g0,g1)
    c: Coincident(g1,g2)
    c: Coincident(g2,g3)
    c: Coincident(g3,g4)
    c: Coincident(g4,g5)
    c: Coincident(g5,g0)
    c: Equal(g0, g1-g5) x5
    c: PointOnObject(g0,g6)
    c: PointOnObject(g1,g6)
    c: PointOnObject(g2,g6)
    c: PointOnObject(g3,g6)
    c: PointOnObject(g4,g6)
    c: PointOnObject(g5,g6)
    c: Coincident(g6,g-1)
    c: Diameter(g6) = 10
    c: PointOnObject(g0,g-2)
    c: Coincident(g7,g8)
    c: Coincident(g8,g9)
    c: Coincident(g9,g10)
    c: Coincident(g10,g11)
    c: Coincident(g11,g12)
    c: Coincident(g12,g7)
    c: Equal(g7, g8-g12) x5
    c: PointOnObject(g7,g13)
    c: PointOnObject(g8,g13)
    c: PointOnObject(g9,g13)
    c: PointOnObject(g10,g13)
    c: PointOnObject(g11,g13)
    c: PointOnObject(g12,g13)
    c: Equal(g13,g6)
    c: Vertical(g7)
    c: Coincident(g0,g14)
    c: Coincident(g14,g8)
    c: Coincident(g14,g15)
    c: Coincident(g15,g16)
    c: Coincident(g16,g14)
    c: Equal(g15,g14)
    c: Equal(g14,g16)
    c: Distance(g16) = 1
    c: Horizontal(g16)
FEATURE [Part::FeaturePython] Array  # Draft array (typed FeaturePython)
  AlwaysSyncPlacement = false
  Angle = 360
  ArrayType = 0
  Axis = (0,0,1)
  Base = -> Sketch004
  Center = (0,0,0)
  Count = 84
  ExpandArray = false
  Fuse = false
  IntervalAxis = (0,0,0)
  IntervalX = (9.5,0,0)
  IntervalY = (0,16.5,0)
  IntervalZ = (0,0,100)
  NumberCircles = 3
  NumberPolar = 5
  NumberX = 14
  NumberY = 6
  NumberZ = 1
  Placement = pos=(2,-45,20) rot=(0,0,1;0rad)
  PlacementList = 84 placements: [(0,0,0),(0,16.5,0),(0,33,0),(0,49.5,0),(0,66,0),(0,82.5,0),(9.5,0,0),(9.5,16.5,0),(9.5,33,0),(9.5,49.5,0),(9.5,66,0),(9.5,82.5,0),(19,0,0),(19,16.5,0),(19,33,0),(19,49.5,0),(19,66,0),(19,82.5,0),(28.5,0,0),(28.5,16.5,0),(28.5,33,0),(28.5,49.5,0),(28.5,66,0),(28.5,82.5,0),(38,0,0),(38,16.5,0),(38,33,0),(38,49.5,0),(38,66,0),(38,82.5,0),(47.5,0,0),(47.5,16.5,0),(47.5,33,0),(47.5,49.5,0),(47.5,66,0),+49 more]
  RadialDistance = 50
  ScaleList = (84) [(1,1,1),(1,1,1),(1,1,1),(1,1,1),(1,1,1),(1,1,1),(1,1,1),(1,1,1),(1,1,1),(1,1,1),(1,1,1),(1,1,1),(1,1,1),(1,1,1),(1,1,1),(1,1,1),(1,1,1),(1,1,1),+66 more]
  Symmetry = 1
  TangentialDistance = 25
FEATURE [Part::Extrusion] Extrude
  Base = -> Array
  Dir = (0,0,1)
  DirMode = 2
  FaceMakerClass = Part::FaceMakerBullseye
  FaceMakerMode = 3
  LengthFwd = 10
  LengthRev = 0
  Placement = pos=(7,8,-4) rot=(0,0,1;0rad)
  Solid = true
  Symmetric = false
